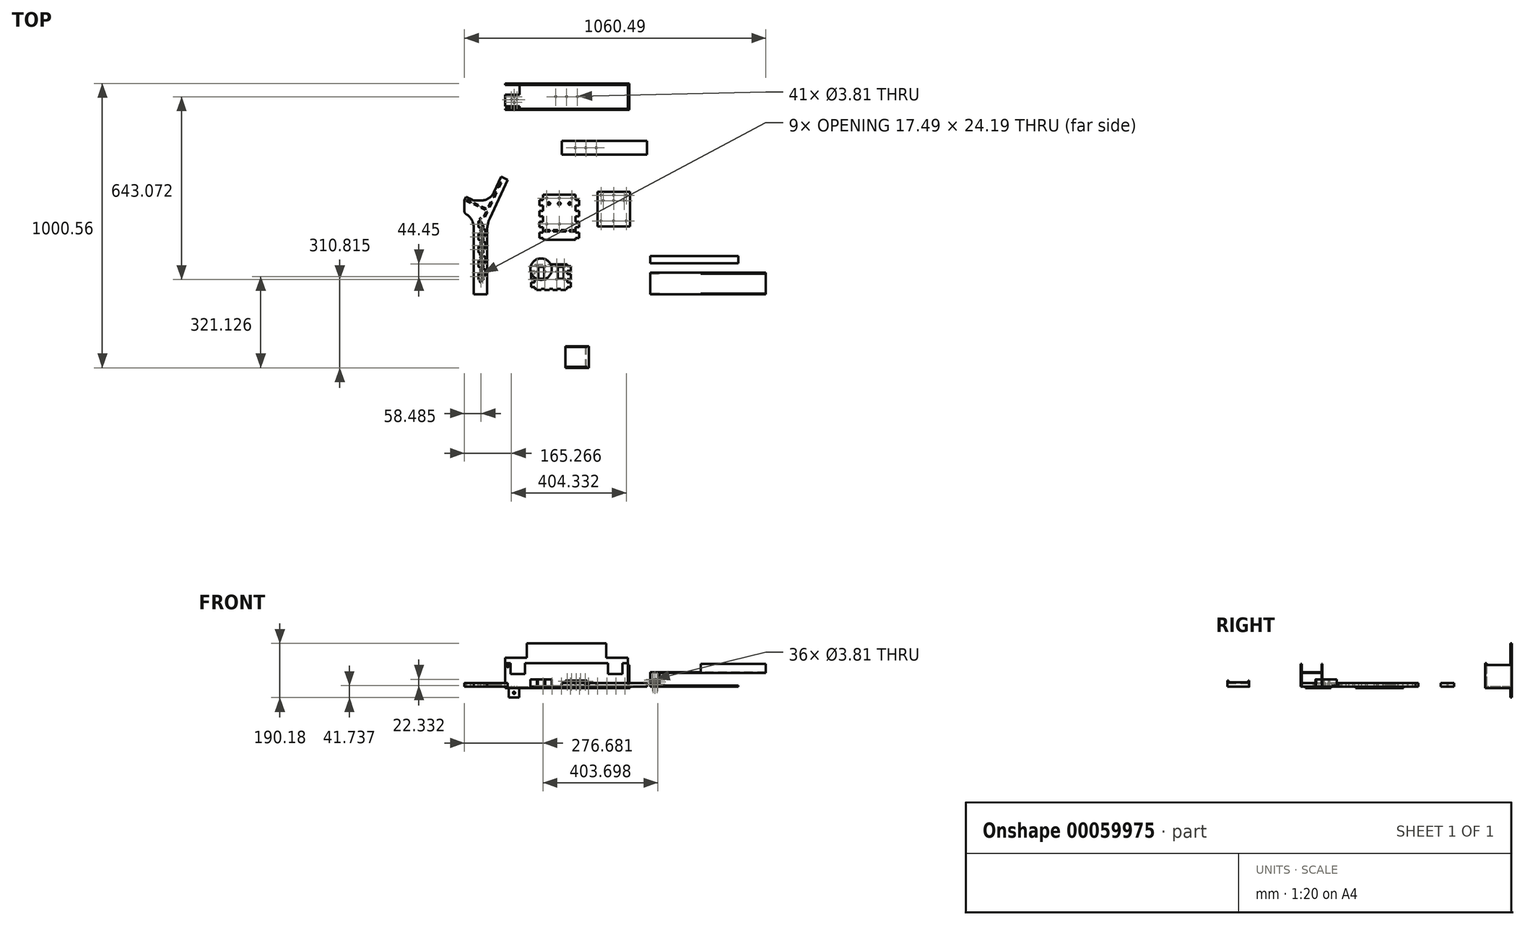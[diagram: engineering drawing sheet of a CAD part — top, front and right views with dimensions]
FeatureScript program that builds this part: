
annotation { "Feature Type Name" : "Feature", "Feature Type Description" : "" }
export const myFeature = defineFeature(function(context is Context, id is Id, definition is map)
    precondition{}
    {
        {
            var Q0;
            Q0=qCreatedBy(makeId("Top.planeOp"),FACE);
            var sketch = newSketch(context, id + "F0", { "sketchPlane" : qUnion([Q0])});
            skLineSegment(sketch, "E0.bottom", {"start": v(0, 0) * mm, "end": v(46.04, 0) * mm});
            skLineSegment(sketch, "E0.top", {"start": v(0, 304.8) * mm, "end": v(46.04, 304.8) * mm});
            skLineSegment(sketch, "E0.left", {"start": v(0, 0) * mm, "end": v(0, 304.8) * mm});
            skLineSegment(sketch, "E0.right", {"start": v(46.04, 0) * mm, "end": v(46.04, 304.8) * mm});
            skSolve(sketch);
        }
        {
            var Q0;
            Q0=makeQuery(id+"F0.imprint","IMPRINT",FACE,{"disambiguationData":[TD([[makeQuery(id+"F0.imprint","IMPRINT",EDGE,{"derivedFrom":sQuery(id+"F0.wireOp",EDGE,"E0.bottom")}),1.0]])]});
            extrude(context, id + "F1", {"entities" : qUnion([Q0]), "depth" : 12.7 * mm});
        }
        {
            var Q0;
            Q0=qCreatedBy(makeId("Top.planeOp"),FACE);
            var sketch = newSketch(context, id + "F2", { "sketchPlane" : qUnion([Q0])});
            skCircle(sketch, "E1", {"center": v(-119.77, 141.64) * mm, "radius": 9.53 * mm});
            skLineSegment(sketch, "E2", {"start": v(-119.77, 132.11) * mm, "end": v(-119.77, 113.06) * mm, "construction": true});
            skLineSegment(sketch, "E3", {"start": v(-119.77, 113.06) * mm, "end": v(-122.95, 113.06) * mm});
            skLineSegment(sketch, "E4", {"start": v(-122.95, 113.06) * mm, "end": v(-129.3, 141.64) * mm});
            skLineSegment(sketch, "E5.MirrorCS", {"start": v(-119.77, 113.06) * mm, "end": v(-116.6, 113.06) * mm});
            skLineSegment(sketch, "E6.MirrorCS", {"start": v(-116.6, 113.06) * mm, "end": v(-110.25, 141.64) * mm});
            skCircle(sketch, "E7", {"center": v(-119.77, 141.64) * mm, "radius": 1.9 * mm});
            skSolve(sketch);
        }
        {
            var Q0;
            Q0=qSketchRegion(id+"F2",true);
            extrude(context, id + "F3", {"entities" : qUnion([Q0]), "depth" : 12.7 * mm});
        }
        {
            var Q0;
            Q0=qCreatedBy(makeId("Top.planeOp"),FACE);
            var sketch = newSketch(context, id + "F4", { "sketchPlane" : qUnion([Q0])});
            skLineSegment(sketch, "E8.bottom", {"start": v(-408.15, 0) * mm, "end": v(-455.78, 0) * mm});
            skLineSegment(sketch, "E8.top", {"start": v(-408.15, 431.8) * mm, "end": v(-455.78, 431.8) * mm});
            skLineSegment(sketch, "E8.left", {"start": v(-408.15, 0) * mm, "end": v(-408.15, 431.8) * mm});
            skLineSegment(sketch, "E8.right", {"start": v(-455.78, 0) * mm, "end": v(-455.78, 279.4) * mm});
            skLineSegment(sketch, "E9", {"start": v(-455.78, 360.5) * mm, "end": v(-455.78, 360.5) * mm});
            skLineSegment(sketch, "E10", {"start": v(-455.78, 360.5) * mm, "end": v(-481.84, 288.89) * mm});
            skLineSegment(sketch, "E11", {"start": v(-481.84, 288.89) * mm, "end": v(-455.78, 279.4) * mm});
            skLineSegment(sketch, "E12", {"start": v(-455.78, 279.4) * mm, "end": v(-455.78, 360.5) * mm});
            skLineSegment(sketch, "E13", {"start": v(-455.78, 279.4) * mm, "end": v(-455.78, 431.8) * mm});
            skSolve(sketch);
        }
        {
            var Q0;
            Q0=makeQuery(id+"F4.imprint","IMPRINT",FACE,{"disambiguationData":[TD([[makeQuery(id+"F4.imprint","IMPRINT",EDGE,{"derivedFrom":sQuery(id+"F4.wireOp",EDGE,"E9")}),1.0]])]});
            var Q1;
            Q1=makeQuery(id+"F4.imprint","IMPRINT",FACE,{"disambiguationData":[TD([[makeQuery(id+"F4.imprint","IMPRINT",EDGE,{"derivedFrom":sQuery(id+"F4.wireOp",EDGE,"E8.bottom")}),-1.0]])]});
            var Q2;
            Q2=makeQuery(id+"F4.imprint","IMPRINT",FACE,{"disambiguationData":[TD([[makeQuery(id+"F4.imprint","IMPRINT",EDGE,{"derivedFrom":sQuery(id+"F4.wireOp",EDGE,"E10")}),1.0]])]});
            extrude(context, id + "F5", {"entities" : qUnion([Q0, Q1, Q2]), "depth" : 12.7 * mm});
        }
        {
            var Q0;
            Q0=makeQuery(id+"F5.opExtrude","SWEPT_FACE",FACE,{"disambiguationData":[OSD([sQuery(id+"F4.wireOp",EDGE,"E8.left")])]});
            var sketch = newSketch(context, id + "F6", { "sketchPlane" : qUnion([Q0])});
            skLineSegment(sketch, "E14.bottom", {"start": v(431.8, 12.7) * mm, "end": v(355.6, 12.7) * mm});
            skLineSegment(sketch, "E14.top", {"start": v(431.8, 0) * mm, "end": v(355.6, 0) * mm});
            skLineSegment(sketch, "E14.left", {"start": v(431.8, 12.7) * mm, "end": v(431.8, 0) * mm});
            skLineSegment(sketch, "E14.right", {"start": v(355.6, 12.7) * mm, "end": v(355.6, 0) * mm});
            skSolve(sketch);
        }
        {
            var Q0;
            Q0=makeQuery(id+"F6.imprint","IMPRINT",FACE,{"disambiguationData":[TD([[makeQuery(id+"F6.imprint","IMPRINT",EDGE,{"derivedFrom":sQuery(id+"F6.wireOp",EDGE,"E14.bottom")}),-1.0]])]});
            extrude(context, id + "F7", {"entities" : qUnion([Q0]), "operationType" : NewBodyOperationType.ADD, "depth" : 6.35 * mm});
        }
        {
            var Q0;
            Q0=makeQuery(id+"F5.opExtrude","CAP_FACE",FACE,{"disambiguationData":[OSD([sQuery(id+"F4.wireOp",EDGE,"E8.bottom"),sQuery(id+"F4.wireOp",EDGE,"E8.top"),sQuery(id+"F4.wireOp",EDGE,"E8.left"),sQuery(id+"F4.wireOp",EDGE,"E8.right"),sQuery(id+"F4.wireOp",EDGE,"E9"),sQuery(id+"F4.wireOp",EDGE,"E10"),sQuery(id+"F4.wireOp",EDGE,"E11")])],"isStart":false});
            var sketch = newSketch(context, id + "F8", { "sketchPlane" : qUnion([Q0])});
            skLineSegment(sketch, "E15", {"start": v(-473.7, 292.68) * mm, "end": v(-470.72, 291.6) * mm});
            skLineSegment(sketch, "E16", {"start": v(-470.72, 291.6) * mm, "end": v(-466.38, 303.53) * mm});
            skLineSegment(sketch, "E17", {"start": v(-466.38, 303.53) * mm, "end": v(-469.36, 304.62) * mm});
            skLineSegment(sketch, "E18", {"start": v(-465.02, 316.55) * mm, "end": v(-462.03, 315.46) * mm});
            skLineSegment(sketch, "E19", {"start": v(-462.03, 315.46) * mm, "end": v(-457.69, 327.4) * mm});
            skLineSegment(sketch, "E20", {"start": v(-457.69, 327.4) * mm, "end": v(-460.67, 328.48) * mm});
            skLineSegment(sketch, "E21", {"start": v(-456.33, 340.42) * mm, "end": v(-453.36, 339.34) * mm});
            skLineSegment(sketch, "E22", {"start": v(-453.36, 339.34) * mm, "end": v(-449.01, 351.27) * mm});
            skLineSegment(sketch, "E23", {"start": v(-449.01, 351.27) * mm, "end": v(-451.9, 352.61) * mm});
            skPoint(sketch, "E24.startSnap0", {"position": v(-459.86, 321.43) * mm});
            skLineSegment(sketch, "E25", {"start": v(-473.7, 292.68) * mm, "end": v(-469.36, 304.62) * mm});
            skLineSegment(sketch, "E26", {"start": v(-465.02, 316.55) * mm, "end": v(-460.67, 328.48) * mm});
            skLineSegment(sketch, "E27", {"start": v(-456.33, 340.42) * mm, "end": v(-451.9, 352.61) * mm});
            skLineSegment(sketch, "E28", {"start": v(-435.45, 314.23) * mm, "end": v(-423.52, 309.9) * mm});
            skLineSegment(sketch, "E29", {"start": v(-435.45, 314.23) * mm, "end": v(-436.54, 311.25) * mm});
            skLineSegment(sketch, "E30", {"start": v(-436.54, 311.25) * mm, "end": v(-424.6, 306.9) * mm});
            skLineSegment(sketch, "E31", {"start": v(-424.6, 306.9) * mm, "end": v(-423.52, 309.9) * mm});
            skLineSegment(sketch, "E32", {"start": v(-453.35, 320.75) * mm, "end": v(-441.42, 316.4) * mm});
            skLineSegment(sketch, "E33", {"start": v(-453.35, 320.75) * mm, "end": v(-454.44, 317.77) * mm});
            skLineSegment(sketch, "E34", {"start": v(-454.44, 317.77) * mm, "end": v(-442.5, 313.42) * mm});
            skLineSegment(sketch, "E35", {"start": v(-442.5, 313.42) * mm, "end": v(-441.42, 316.4) * mm});
            skLineSegment(sketch, "E36", {"start": v(-417.55, 307.72) * mm, "end": v(-405.61, 303.38) * mm});
            skLineSegment(sketch, "E37", {"start": v(-417.55, 307.72) * mm, "end": v(-418.63, 304.74) * mm});
            skLineSegment(sketch, "E38", {"start": v(-418.63, 304.74) * mm, "end": v(-406.7, 300.4) * mm});
            skLineSegment(sketch, "E39", {"start": v(-406.7, 300.4) * mm, "end": v(-405.61, 303.38) * mm});
            skSolve(sketch);
        }
        {
            var Q0;
            Q0=qSketchRegion(id+"F8",true);
            extrude(context, id + "F9", {"entities" : qUnion([Q0]), "operationType" : NewBodyOperationType.REMOVE, "endBound" : BoundingType.UP_TO_NEXT, "oppositeDirection" : true, "depth" : 25.4 * mm});
        }
        {
            var Q0;
            Q0=qCreatedBy(makeId("Top.planeOp"),FACE);
            var sketch = newSketch(context, id + "F10", { "sketchPlane" : qUnion([Q0])});
            skLineSegment(sketch, "E40.bottom", {"start": v(-574.22, 0) * mm, "end": v(-621.84, 0) * mm});
            skLineSegment(sketch, "E40.top", {"start": v(-574.22, 330.2) * mm, "end": v(-621.84, 330.2) * mm});
            skLineSegment(sketch, "E40.left", {"start": v(-574.22, 0) * mm, "end": v(-574.22, 330.2) * mm});
            skLineSegment(sketch, "E40.right", {"start": v(-621.84, 0) * mm, "end": v(-621.84, 330.2) * mm});
            skLineSegment(sketch, "E41", {"start": v(-574.22, 247.83) * mm, "end": v(-501.76, 403.22) * mm});
            skLineSegment(sketch, "E42", {"start": v(-501.76, 403.22) * mm, "end": v(-524.78, 413.95) * mm});
            skLineSegment(sketch, "E43", {"start": v(-524.78, 413.95) * mm, "end": v(-563.84, 330.2) * mm});
            skCircle(sketch, "E44", {"center": v(-598.03, 266.7) * mm, "radius": 1.84 * mm});
            skCircle(sketch, "E45", {"center": v(-598.03, 139.7) * mm, "radius": 1.84 * mm});
            skCircle(sketch, "E46", {"center": v(-598.03, 44.45) * mm, "radius": 1.84 * mm});
            skLineSegment(sketch, "E47", {"start": v(-574.22, 165.1) * mm, "end": v(-621.84, 165.1) * mm, "construction": true});
            skLineSegment(sketch, "E48", {"start": v(-574.22, 247.83) * mm, "end": v(-671.77, 293.32) * mm});
            skLineSegment(sketch, "E49", {"start": v(-671.77, 293.32) * mm, "end": v(-648.73, 342.73) * mm});
            skLineSegment(sketch, "E50", {"start": v(-648.73, 342.73) * mm, "end": v(-621.84, 330.2) * mm});
            skLineSegment(sketch, "E51", {"start": v(-598.03, 330.2) * mm, "end": v(-598.03, 0) * mm, "construction": true});
            skLineSegment(sketch, "E52", {"start": v(-654.1, 331.22) * mm, "end": v(-654.1, 285.08) * mm});
            skLineSegment(sketch, "E53", {"start": v(-574.22, 330.2) * mm, "end": v(-563.84, 330.2) * mm});
            skSolve(sketch);
        }
        {
            var Q0;
            {var subQ0=sQuery(id+"F10.wireOp",EDGE,"E50");Q0=makeQuery(id+"F10.imprint","IMPRINT",FACE,{"disambiguationData":[TD([[makeQuery(id+"F10.imprint","IMPRINT",EDGE,{"derivedFrom":subQ0}),-1.0]])]});}
            var Q1;
            Q1=makeQuery(id+"F10.imprint","IMPRINT",FACE,{"disambiguationData":[TD([[makeQuery(id+"F10.imprint","IMPRINT",EDGE,{"derivedFrom":sQuery(id+"F10.wireOp",EDGE,"E44")}),-1.0]])]});
            var Q2;
            {var subQ0=sQuery(id+"F10.wireOp",EDGE,"E41");Q2=makeQuery(id+"F10.imprint","IMPRINT",FACE,{"disambiguationData":[TD([[makeQuery(id+"F10.imprint","IMPRINT",EDGE,{"derivedFrom":subQ0}),1.0]])]});}
            var Q3;
            {var subQ1=sQuery(id+"F10.wireOp",EDGE,"E40.bottom");Q3=makeQuery(id+"F10.imprint","IMPRINT",FACE,{"disambiguationData":[TD([[makeQuery(id+"F10.imprint","IMPRINT",EDGE,{"derivedFrom":subQ1}),-1.0]])]});}
            extrude(context, id + "F11", {"entities" : qUnion([Q0, Q1, Q2, Q3]), "depth" : 12.7 * mm});
        }
        {
            var Q0;
            Q0=makeQuery(id+"F5.opExtrude","SWEPT_BODY",BODY,{"disambiguationData":[OSD([sQuery(id+"F4.wireOp",EDGE,"E8.bottom"),sQuery(id+"F4.wireOp",EDGE,"E8.top"),sQuery(id+"F4.wireOp",EDGE,"E8.left"),sQuery(id+"F4.wireOp",EDGE,"E8.right"),sQuery(id+"F4.wireOp",EDGE,"E10"),sQuery(id+"F4.wireOp",EDGE,"E11"),sQuery(id+"F4.wireOp",EDGE,"E13")])]});
            deleteBodies(context, id + "F12", {"entities" : qUnion([Q0])});
        }
        {
            var Q0;
            Q0=makeQuery(id+"F11.opExtrude","CAP_FACE",FACE,{"disambiguationData":[OSD([sQuery(id+"F10.wireOp",EDGE,"E40.bottom"),sQuery(id+"F10.wireOp",EDGE,"E40.top"),sQuery(id+"F10.wireOp",EDGE,"E40.left"),sQuery(id+"F10.wireOp",EDGE,"E40.right"),sQuery(id+"F10.wireOp",EDGE,"Y91T5dXO-O9do-Qezp-Nh4v-n6mu9yF64eSj"),sQuery(id+"F10.wireOp",EDGE,"wk8H9K5M-Q0OB-IsqO-xqjk-N4ZivMZWohHq"),sQuery(id+"F10.wireOp",EDGE,"1UNdf9ru-KzUG-1IXl-ZwoR-ekO7E109dlTN"),sQuery(id+"F10.wireOp",EDGE,"abHQwaP6-kXHW-M4Kr-ZBDh-lSKwXKwhMN8O")])],"isStart":false});
            var sketch = newSketch(context, id + "F13", { "sketchPlane" : qUnion([Q0])});
            skLineSegment(sketch, "E54.bottom", {"start": v(-604.35, 88.9) * mm, "end": v(-580.57, 88.9) * mm});
            skLineSegment(sketch, "E54.top", {"start": v(-604.35, 50.8) * mm, "end": v(-580.57, 50.8) * mm});
            skLineSegment(sketch, "E54.left", {"start": v(-604.35, 88.9) * mm, "end": v(-604.35, 50.8) * mm});
            skLineSegment(sketch, "E54.right", {"start": v(-580.57, 88.9) * mm, "end": v(-580.57, 50.8) * mm});
            skLineSegment(sketch, "E55", {"start": v(-604.35, 82.9) * mm, "end": v(-584.31, 50.8) * mm});
            skLineSegment(sketch, "E56", {"start": v(-600.6, 88.9) * mm, "end": v(-580.57, 56.8) * mm});
            skLineSegment(sketch, "E57.0.1.0", {"start": v(-604.35, 133.35) * mm, "end": v(-580.57, 133.35) * mm});
            skLineSegment(sketch, "E57.0.1.1", {"start": v(-580.57, 133.35) * mm, "end": v(-580.57, 95.25) * mm});
            skLineSegment(sketch, "E57.0.1.2", {"start": v(-604.35, 127.35) * mm, "end": v(-584.31, 95.25) * mm});
            skLineSegment(sketch, "E57.0.1.3", {"start": v(-604.35, 95.25) * mm, "end": v(-580.57, 95.25) * mm});
            skLineSegment(sketch, "E57.0.1.4", {"start": v(-604.35, 133.35) * mm, "end": v(-604.35, 95.25) * mm});
            skLineSegment(sketch, "E57.0.1.5", {"start": v(-600.6, 133.35) * mm, "end": v(-580.57, 101.25) * mm});
            skLineSegment(sketch, "E57.direction1", {"start": v(-604.35, 88.9) * mm, "end": v(-529.02, 88.9) * mm, "construction": true});
            skLineSegment(sketch, "E57.direction2", {"start": v(-604.35, 88.9) * mm, "end": v(-604.35, 133.35) * mm, "construction": true});
            skLineSegment(sketch, "E58.0.1.0", {"start": v(-604.35, 184.15) * mm, "end": v(-580.57, 184.15) * mm});
            skLineSegment(sketch, "E58.0.1.1", {"start": v(-580.57, 184.15) * mm, "end": v(-580.57, 146.05) * mm});
            skLineSegment(sketch, "E58.0.1.2", {"start": v(-604.35, 178.15) * mm, "end": v(-584.31, 146.05) * mm});
            skLineSegment(sketch, "E58.0.1.3", {"start": v(-604.35, 146.05) * mm, "end": v(-580.57, 146.05) * mm});
            skLineSegment(sketch, "E58.0.1.4", {"start": v(-604.35, 184.15) * mm, "end": v(-604.35, 146.05) * mm});
            skLineSegment(sketch, "E58.0.1.5", {"start": v(-600.6, 184.15) * mm, "end": v(-580.57, 152.05) * mm});
            skLineSegment(sketch, "E58.0.1.6", {"start": v(-604.35, 139.7) * mm, "end": v(-604.35, 184.15) * mm, "construction": true});
            skLineSegment(sketch, "E58.direction1", {"start": v(-604.35, 133.35) * mm, "end": v(-529.02, 133.35) * mm, "construction": true});
            skLineSegment(sketch, "E58.direction2", {"start": v(-604.35, 133.35) * mm, "end": v(-604.35, 184.15) * mm, "construction": true});
            skLineSegment(sketch, "E59.0.1.0", {"start": v(-604.35, 228.6) * mm, "end": v(-580.57, 228.6) * mm});
            skLineSegment(sketch, "E59.0.1.1", {"start": v(-600.6, 228.6) * mm, "end": v(-580.57, 196.5) * mm});
            skLineSegment(sketch, "E59.0.1.2", {"start": v(-580.57, 228.6) * mm, "end": v(-580.57, 190.5) * mm});
            skLineSegment(sketch, "E59.0.1.3", {"start": v(-604.35, 190.5) * mm, "end": v(-580.57, 190.5) * mm});
            skLineSegment(sketch, "E59.0.1.4", {"start": v(-604.35, 228.6) * mm, "end": v(-604.35, 190.5) * mm});
            skLineSegment(sketch, "E59.0.1.5", {"start": v(-604.35, 222.6) * mm, "end": v(-584.31, 190.5) * mm});
            skLineSegment(sketch, "E59.0.2.0", {"start": v(-604.35, 273.05) * mm, "end": v(-580.57, 273.05) * mm});
            skLineSegment(sketch, "E59.0.2.1", {"start": v(-600.6, 273.05) * mm, "end": v(-580.57, 240.95) * mm});
            skLineSegment(sketch, "E59.0.2.2", {"start": v(-580.57, 273.05) * mm, "end": v(-580.57, 234.95) * mm});
            skLineSegment(sketch, "E59.0.2.3", {"start": v(-604.35, 234.95) * mm, "end": v(-580.57, 234.95) * mm});
            skLineSegment(sketch, "E59.0.2.4", {"start": v(-604.35, 273.05) * mm, "end": v(-604.35, 234.95) * mm});
            skLineSegment(sketch, "E59.0.2.5", {"start": v(-604.35, 267.05) * mm, "end": v(-584.31, 234.95) * mm});
            skLineSegment(sketch, "E59.direction1", {"start": v(-604.35, 184.15) * mm, "end": v(-529.02, 184.15) * mm, "construction": true});
            skLineSegment(sketch, "E59.direction2", {"start": v(-604.35, 184.15) * mm, "end": v(-604.35, 228.6) * mm, "construction": true});
            skSolve(sketch);
        }
        {
            var Q0;
            {var subQ3=sQuery(id+"F13.wireOp",EDGE,"E59.0.2.5");Q0=makeQuery(id+"F13.imprint","IMPRINT",FACE,{"disambiguationData":[TD([[makeQuery(id+"F13.imprint","IMPRINT",EDGE,{"derivedFrom":subQ3}),-1.0]])]});}
            var Q1;
            {var subQ3=sQuery(id+"F13.wireOp",EDGE,"E59.0.1.1");Q1=makeQuery(id+"F13.imprint","IMPRINT",FACE,{"disambiguationData":[TD([[makeQuery(id+"F13.imprint","IMPRINT",EDGE,{"derivedFrom":subQ3}),1.0]])]});}
            var Q2;
            {var subQ3=sQuery(id+"F13.wireOp",EDGE,"E59.0.1.5");Q2=makeQuery(id+"F13.imprint","IMPRINT",FACE,{"disambiguationData":[TD([[makeQuery(id+"F13.imprint","IMPRINT",EDGE,{"derivedFrom":subQ3}),-1.0]])]});}
            var Q3;
            {var subQ3=sQuery(id+"F13.wireOp",EDGE,"E58.0.1.5");Q3=makeQuery(id+"F13.imprint","IMPRINT",FACE,{"disambiguationData":[TD([[makeQuery(id+"F13.imprint","IMPRINT",EDGE,{"derivedFrom":subQ3}),1.0]])]});}
            var Q4;
            {var subQ0=sQuery(id+"F13.wireOp",EDGE,"E58.0.1.2");Q4=makeQuery(id+"F13.imprint","IMPRINT",FACE,{"disambiguationData":[TD([[makeQuery(id+"F13.imprint","IMPRINT",EDGE,{"derivedFrom":subQ0}),-1.0]])]});}
            var Q5;
            {var subQ3=sQuery(id+"F13.wireOp",EDGE,"E57.0.1.5");Q5=makeQuery(id+"F13.imprint","IMPRINT",FACE,{"disambiguationData":[TD([[makeQuery(id+"F13.imprint","IMPRINT",EDGE,{"derivedFrom":subQ3}),1.0]])]});}
            var Q6;
            {var subQ0=sQuery(id+"F13.wireOp",EDGE,"E57.0.1.2");Q6=makeQuery(id+"F13.imprint","IMPRINT",FACE,{"disambiguationData":[TD([[makeQuery(id+"F13.imprint","IMPRINT",EDGE,{"derivedFrom":subQ0}),-1.0]])]});}
            var Q7;
            {var subQ3=sQuery(id+"F13.wireOp",EDGE,"E56");Q7=makeQuery(id+"F13.imprint","IMPRINT",FACE,{"disambiguationData":[TD([[makeQuery(id+"F13.imprint","IMPRINT",EDGE,{"derivedFrom":subQ3}),1.0]])]});}
            var Q8;
            {var subQ3=sQuery(id+"F13.wireOp",EDGE,"E55");Q8=makeQuery(id+"F13.imprint","IMPRINT",FACE,{"disambiguationData":[TD([[makeQuery(id+"F13.imprint","IMPRINT",EDGE,{"derivedFrom":subQ3}),-1.0]])]});}
            extrude(context, id + "F14", {"entities" : qUnion([Q0, Q1, Q2, Q3, Q4, Q5, Q6, Q7, Q8]), "operationType" : NewBodyOperationType.REMOVE, "endBound" : BoundingType.UP_TO_NEXT, "oppositeDirection" : true, "depth" : 25.4 * mm});
        }
        {
            var Q0;
            Q0=makeQuery(id+"F14.boolean.opBoolean","COPY",EDGE,{"derivedFrom":makeQuery(id+"F14.opExtrude","SWEPT_EDGE",EDGE,{"disambiguationData":[OSD([sQuery(id+"F13.wireOp",EDGE,"E59.0.2.3"),sQuery(id+"F13.wireOp",EDGE,"E59.0.2.4")])]})});
            var Q1;
            Q1=makeQuery(id+"F14.boolean.opBoolean","COPY",EDGE,{"derivedFrom":makeQuery(id+"F14.opExtrude","SWEPT_EDGE",EDGE,{"disambiguationData":[OSD([sQuery(id+"F13.wireOp",EDGE,"E59.0.1.3"),sQuery(id+"F13.wireOp",EDGE,"E59.0.1.4")])]})});
            var Q2;
            Q2=makeQuery(id+"F14.boolean.opBoolean","COPY",EDGE,{"derivedFrom":makeQuery(id+"F14.opExtrude","SWEPT_EDGE",EDGE,{"disambiguationData":[OSD([sQuery(id+"F13.wireOp",EDGE,"E58.0.1.3"),sQuery(id+"F13.wireOp",EDGE,"E58.0.1.4")])]})});
            var Q3;
            Q3=makeQuery(id+"F14.boolean.opBoolean","COPY",EDGE,{"derivedFrom":makeQuery(id+"F14.opExtrude","SWEPT_EDGE",EDGE,{"disambiguationData":[OSD([sQuery(id+"F13.wireOp",EDGE,"E57.0.1.3"),sQuery(id+"F13.wireOp",EDGE,"E57.0.1.4")])]})});
            var Q4;
            Q4=makeQuery(id+"F14.boolean.opBoolean","COPY",EDGE,{"derivedFrom":makeQuery(id+"F14.opExtrude","SWEPT_EDGE",EDGE,{"disambiguationData":[OSD([sQuery(id+"F13.wireOp",EDGE,"E54.top"),sQuery(id+"F13.wireOp",EDGE,"E54.left")])]})});
            var Q5;
            Q5=makeQuery(id+"F14.boolean.opBoolean","COPY",EDGE,{"derivedFrom":makeQuery(id+"F14.opExtrude","SWEPT_EDGE",EDGE,{"disambiguationData":[OSD([sQuery(id+"F13.wireOp",EDGE,"E54.left"),sQuery(id+"F13.wireOp",EDGE,"E55")])]})});
            var Q6;
            Q6=makeQuery(id+"F14.boolean.opBoolean","COPY",EDGE,{"derivedFrom":makeQuery(id+"F14.opExtrude","SWEPT_EDGE",EDGE,{"disambiguationData":[OSD([sQuery(id+"F13.wireOp",EDGE,"E57.0.1.2"),sQuery(id+"F13.wireOp",EDGE,"E57.0.1.4")])]})});
            var Q7;
            Q7=makeQuery(id+"F14.boolean.opBoolean","COPY",EDGE,{"derivedFrom":makeQuery(id+"F14.opExtrude","SWEPT_EDGE",EDGE,{"disambiguationData":[OSD([sQuery(id+"F13.wireOp",EDGE,"E58.0.1.2"),sQuery(id+"F13.wireOp",EDGE,"E58.0.1.4")])]})});
            var Q8;
            Q8=makeQuery(id+"F14.boolean.opBoolean","COPY",EDGE,{"derivedFrom":makeQuery(id+"F14.opExtrude","SWEPT_EDGE",EDGE,{"disambiguationData":[OSD([sQuery(id+"F13.wireOp",EDGE,"E59.0.1.4"),sQuery(id+"F13.wireOp",EDGE,"E59.0.1.5")])]})});
            var Q9;
            Q9=makeQuery(id+"F14.boolean.opBoolean","COPY",EDGE,{"derivedFrom":makeQuery(id+"F14.opExtrude","SWEPT_EDGE",EDGE,{"disambiguationData":[OSD([sQuery(id+"F13.wireOp",EDGE,"E59.0.2.4"),sQuery(id+"F13.wireOp",EDGE,"E59.0.2.5")])]})});
            var Q10;
            Q10=makeQuery(id+"F14.boolean.opBoolean","COPY",EDGE,{"derivedFrom":makeQuery(id+"F14.opExtrude","SWEPT_EDGE",EDGE,{"disambiguationData":[OSD([sQuery(id+"F13.wireOp",EDGE,"E54.bottom"),sQuery(id+"F13.wireOp",EDGE,"E54.right")])]})});
            var Q11;
            Q11=makeQuery(id+"F14.boolean.opBoolean","COPY",EDGE,{"derivedFrom":makeQuery(id+"F14.opExtrude","SWEPT_EDGE",EDGE,{"disambiguationData":[OSD([sQuery(id+"F13.wireOp",EDGE,"E57.0.1.0"),sQuery(id+"F13.wireOp",EDGE,"E57.0.1.1")])]})});
            var Q12;
            Q12=makeQuery(id+"F14.boolean.opBoolean","COPY",EDGE,{"derivedFrom":makeQuery(id+"F14.opExtrude","SWEPT_EDGE",EDGE,{"disambiguationData":[OSD([sQuery(id+"F13.wireOp",EDGE,"E58.0.1.0"),sQuery(id+"F13.wireOp",EDGE,"E58.0.1.1")])]})});
            var Q13;
            Q13=makeQuery(id+"F14.boolean.opBoolean","COPY",EDGE,{"derivedFrom":makeQuery(id+"F14.opExtrude","SWEPT_EDGE",EDGE,{"disambiguationData":[OSD([sQuery(id+"F13.wireOp",EDGE,"E59.0.1.0"),sQuery(id+"F13.wireOp",EDGE,"E59.0.1.2")])]})});
            var Q14;
            Q14=makeQuery(id+"F14.boolean.opBoolean","COPY",EDGE,{"derivedFrom":makeQuery(id+"F14.opExtrude","SWEPT_EDGE",EDGE,{"disambiguationData":[OSD([sQuery(id+"F13.wireOp",EDGE,"E59.0.1.1"),sQuery(id+"F13.wireOp",EDGE,"E59.0.1.2")])]})});
            var Q15;
            Q15=makeQuery(id+"F14.boolean.opBoolean","COPY",EDGE,{"derivedFrom":makeQuery(id+"F14.opExtrude","SWEPT_EDGE",EDGE,{"disambiguationData":[OSD([sQuery(id+"F13.wireOp",EDGE,"E58.0.1.1"),sQuery(id+"F13.wireOp",EDGE,"E58.0.1.5")])]})});
            var Q16;
            Q16=makeQuery(id+"F14.boolean.opBoolean","COPY",EDGE,{"derivedFrom":makeQuery(id+"F14.opExtrude","SWEPT_EDGE",EDGE,{"disambiguationData":[OSD([sQuery(id+"F13.wireOp",EDGE,"E57.0.1.1"),sQuery(id+"F13.wireOp",EDGE,"E57.0.1.5")])]})});
            var Q17;
            Q17=makeQuery(id+"F14.boolean.opBoolean","COPY",EDGE,{"derivedFrom":makeQuery(id+"F14.opExtrude","SWEPT_EDGE",EDGE,{"disambiguationData":[OSD([sQuery(id+"F13.wireOp",EDGE,"E54.right"),sQuery(id+"F13.wireOp",EDGE,"E56")])]})});
            var Q18;
            Q18=makeQuery(id+"F14.boolean.opBoolean","COPY",EDGE,{"derivedFrom":makeQuery(id+"F14.opExtrude","SWEPT_EDGE",EDGE,{"disambiguationData":[OSD([sQuery(id+"F13.wireOp",EDGE,"E54.top"),sQuery(id+"F13.wireOp",EDGE,"E55")])]})});
            var Q19;
            Q19=makeQuery(id+"F14.boolean.opBoolean","COPY",EDGE,{"derivedFrom":makeQuery(id+"F14.opExtrude","SWEPT_EDGE",EDGE,{"disambiguationData":[OSD([sQuery(id+"F13.wireOp",EDGE,"E57.0.1.2"),sQuery(id+"F13.wireOp",EDGE,"E57.0.1.3")])]})});
            var Q20;
            Q20=makeQuery(id+"F14.boolean.opBoolean","COPY",EDGE,{"derivedFrom":makeQuery(id+"F14.opExtrude","SWEPT_EDGE",EDGE,{"disambiguationData":[OSD([sQuery(id+"F13.wireOp",EDGE,"E58.0.1.2"),sQuery(id+"F13.wireOp",EDGE,"E58.0.1.3")])]})});
            var Q21;
            Q21=makeQuery(id+"F14.boolean.opBoolean","COPY",EDGE,{"derivedFrom":makeQuery(id+"F14.opExtrude","SWEPT_EDGE",EDGE,{"disambiguationData":[OSD([sQuery(id+"F13.wireOp",EDGE,"E59.0.1.3"),sQuery(id+"F13.wireOp",EDGE,"E59.0.1.5")])]})});
            var Q22;
            Q22=makeQuery(id+"F14.boolean.opBoolean","COPY",EDGE,{"derivedFrom":makeQuery(id+"F14.opExtrude","SWEPT_EDGE",EDGE,{"disambiguationData":[OSD([sQuery(id+"F13.wireOp",EDGE,"E59.0.2.3"),sQuery(id+"F13.wireOp",EDGE,"E59.0.2.5")])]})});
            var Q23;
            Q23=makeQuery(id+"F14.boolean.opBoolean","COPY",EDGE,{"derivedFrom":makeQuery(id+"F14.opExtrude","SWEPT_EDGE",EDGE,{"disambiguationData":[OSD([sQuery(id+"F13.wireOp",EDGE,"E54.bottom"),sQuery(id+"F13.wireOp",EDGE,"E56")])]})});
            var Q24;
            Q24=makeQuery(id+"F14.boolean.opBoolean","COPY",EDGE,{"derivedFrom":makeQuery(id+"F14.opExtrude","SWEPT_EDGE",EDGE,{"disambiguationData":[OSD([sQuery(id+"F13.wireOp",EDGE,"E57.0.1.0"),sQuery(id+"F13.wireOp",EDGE,"E57.0.1.5")])]})});
            var Q25;
            Q25=makeQuery(id+"F14.boolean.opBoolean","COPY",EDGE,{"derivedFrom":makeQuery(id+"F14.opExtrude","SWEPT_EDGE",EDGE,{"disambiguationData":[OSD([sQuery(id+"F13.wireOp",EDGE,"E58.0.1.0"),sQuery(id+"F13.wireOp",EDGE,"E58.0.1.5")])]})});
            var Q26;
            Q26=makeQuery(id+"F14.boolean.opBoolean","COPY",EDGE,{"derivedFrom":makeQuery(id+"F14.opExtrude","SWEPT_EDGE",EDGE,{"disambiguationData":[OSD([sQuery(id+"F13.wireOp",EDGE,"E59.0.1.0"),sQuery(id+"F13.wireOp",EDGE,"E59.0.1.1")])]})});
            fillet(context, id + "F15", {"entities" : qUnion([Q0, Q1, Q2, Q3, Q4, Q5, Q6, Q7, Q8, Q9, Q10, Q11, Q12, Q13, Q14, Q15, Q16, Q17, Q18, Q19, Q20, Q21, Q22, Q23, Q24, Q25, Q26]), "radius" : 3.17 * mm, "tangentPropagation" : true, "allowEdgeOverflow" : false});
        }
        {
            var Q0;
            Q0=makeQuery(id+"F1.opExtrude","SWEPT_BODY",BODY,{"disambiguationData":[OSD([sQuery(id+"F0.wireOp",EDGE,"E0.bottom"),sQuery(id+"F0.wireOp",EDGE,"E0.top"),sQuery(id+"F0.wireOp",EDGE,"E0.left"),sQuery(id+"F0.wireOp",EDGE,"E0.right")])]});
            var Q1;
            Q1=makeQuery(id+"F1OaYgbKn4OfgPz_1.opExtrude","SWEPT_BODY",BODY,{"disambiguationData":[OSD([sQuery(id+"FSCGUaJBi3wnmaW_1.wireOp",EDGE,"10d2bce9-ad60-4194-9a44-aa3babc14cea.bottom"),sQuery(id+"FSCGUaJBi3wnmaW_1.wireOp",EDGE,"10d2bce9-ad60-4194-9a44-aa3babc14cea.top"),sQuery(id+"FSCGUaJBi3wnmaW_1.wireOp",EDGE,"10d2bce9-ad60-4194-9a44-aa3babc14cea.left"),sQuery(id+"FSCGUaJBi3wnmaW_1.wireOp",EDGE,"10d2bce9-ad60-4194-9a44-aa3babc14cea.right")])]});
            var Q2;
            Q2=makeQuery(id+"F3.opExtrude","SWEPT_BODY",BODY,{"disambiguationData":[OSD([sQuery(id+"F2.wireOp",EDGE,"E1"),sQuery(id+"F2.wireOp",EDGE,"E3"),sQuery(id+"F2.wireOp",EDGE,"E4"),sQuery(id+"F2.wireOp",EDGE,"E5.MirrorCS"),sQuery(id+"F2.wireOp",EDGE,"E6.MirrorCS"),sQuery(id+"F2.wireOp",EDGE,"E7")])]});
            deleteBodies(context, id + "F16", {"entities" : qUnion([Q0, Q1, Q2])});
        }
        {
            var Q0;
            Q0=makeQuery(id+"F11.opExtrude","CAP_FACE",FACE,{"disambiguationData":[OSD([sQuery(id+"F10.wireOp",EDGE,"E40.bottom"),sQuery(id+"F10.wireOp",EDGE,"E40.left"),sQuery(id+"F10.wireOp",EDGE,"E40.right"),sQuery(id+"F10.wireOp",EDGE,"E41"),sQuery(id+"F10.wireOp",EDGE,"E42"),sQuery(id+"F10.wireOp",EDGE,"E43"),sQuery(id+"F10.wireOp",EDGE,"E44"),sQuery(id+"F10.wireOp",EDGE,"E45"),sQuery(id+"F10.wireOp",EDGE,"E46")])],"isStart":false});
            var sketch = newSketch(context, id + "F17", { "sketchPlane" : qUnion([Q0])});
            skLineSegment(sketch, "E60", {"start": v(-519.03, 411.27) * mm, "end": v(-634.58, 163.46) * mm, "construction": true});
            skLineSegment(sketch, "E61", {"start": v(-527.08, 394) * mm, "end": v(-529.06, 394.93) * mm});
            skLineSegment(sketch, "E62", {"start": v(-529.06, 394.93) * mm, "end": v(-537.1, 377.66) * mm});
            skLineSegment(sketch, "E63", {"start": v(-537.1, 377.66) * mm, "end": v(-535.13, 376.74) * mm});
            skLineSegment(sketch, "E64.MirrorCS", {"start": v(-525.1, 393.08) * mm, "end": v(-533.15, 375.82) * mm});
            skLineSegment(sketch, "E65.MirrorCS", {"start": v(-527.08, 394) * mm, "end": v(-525.1, 393.08) * mm});
            skLineSegment(sketch, "E66.MirrorCS", {"start": v(-533.15, 375.82) * mm, "end": v(-535.13, 376.74) * mm});
            skLineSegment(sketch, "E67.1.0.0", {"start": v(-545.16, 360.4) * mm, "end": v(-553.2, 343.13) * mm});
            skLineSegment(sketch, "E67.1.0.1", {"start": v(-543.18, 359.48) * mm, "end": v(-545.16, 360.4) * mm});
            skLineSegment(sketch, "E67.1.0.2", {"start": v(-543.18, 359.48) * mm, "end": v(-541.2, 358.55) * mm});
            skLineSegment(sketch, "E67.1.0.3", {"start": v(-541.2, 358.55) * mm, "end": v(-549.25, 341.29) * mm});
            skLineSegment(sketch, "E67.1.0.4", {"start": v(-549.25, 341.29) * mm, "end": v(-551.23, 342.21) * mm});
            skLineSegment(sketch, "E67.1.0.5", {"start": v(-553.2, 343.13) * mm, "end": v(-551.23, 342.21) * mm});
            skLineSegment(sketch, "E67.2.0.0", {"start": v(-561.26, 325.87) * mm, "end": v(-569.31, 308.6) * mm});
            skLineSegment(sketch, "E67.2.0.1", {"start": v(-559.28, 324.95) * mm, "end": v(-561.26, 325.87) * mm});
            skLineSegment(sketch, "E67.2.0.2", {"start": v(-559.28, 324.95) * mm, "end": v(-557.3, 324.02) * mm});
            skLineSegment(sketch, "E67.2.0.3", {"start": v(-557.3, 324.02) * mm, "end": v(-565.35, 306.76) * mm});
            skLineSegment(sketch, "E67.2.0.4", {"start": v(-565.35, 306.76) * mm, "end": v(-567.33, 307.68) * mm});
            skLineSegment(sketch, "E67.2.0.5", {"start": v(-569.31, 308.6) * mm, "end": v(-567.33, 307.68) * mm});
            skLineSegment(sketch, "E67.direction1", {"start": v(-537.1, 377.66) * mm, "end": v(-553.2, 343.13) * mm, "construction": true});
            skLineSegment(sketch, "E68.0.3.0", {"start": v(-577.36, 291.34) * mm, "end": v(-585.41, 274.07) * mm});
            skLineSegment(sketch, "E68.3.3.0", {"start": v(-575.38, 290.41) * mm, "end": v(-577.36, 291.34) * mm});
            skLineSegment(sketch, "E68.6.3.0", {"start": v(-575.38, 290.41) * mm, "end": v(-573.4, 289.5) * mm});
            skLineSegment(sketch, "E68.9.3.0", {"start": v(-573.4, 289.5) * mm, "end": v(-581.46, 272.23) * mm});
            skLineSegment(sketch, "E68.12.3.0", {"start": v(-581.46, 272.23) * mm, "end": v(-583.43, 273.15) * mm});
            skLineSegment(sketch, "E68.15.3.0", {"start": v(-585.41, 274.07) * mm, "end": v(-583.43, 273.15) * mm});
            skLineSegment(sketch, "E69", {"start": v(-652.75, 334.1) * mm, "end": v(-555.2, 288.61) * mm, "construction": true});
            skLineSegment(sketch, "E70", {"start": v(-595.2, 307.27) * mm, "end": v(-594.28, 309.24) * mm});
            skLineSegment(sketch, "E71", {"start": v(-594.28, 309.24) * mm, "end": v(-578.74, 302) * mm});
            skLineSegment(sketch, "E72", {"start": v(-578.74, 302) * mm, "end": v(-579.66, 300.02) * mm});
            skLineSegment(sketch, "E73.MirrorCS", {"start": v(-596.12, 305.29) * mm, "end": v(-580.58, 298.04) * mm});
            skLineSegment(sketch, "E74.MirrorCS", {"start": v(-580.58, 298.04) * mm, "end": v(-579.66, 300.02) * mm});
            skLineSegment(sketch, "E75.MirrorCS", {"start": v(-595.2, 307.27) * mm, "end": v(-596.12, 305.29) * mm});
            skLineSegment(sketch, "E76.1.0.0", {"start": v(-620.18, 321.32) * mm, "end": v(-604.64, 314.07) * mm});
            skLineSegment(sketch, "E76.1.0.1", {"start": v(-621.1, 319.34) * mm, "end": v(-620.18, 321.32) * mm});
            skLineSegment(sketch, "E76.1.0.2", {"start": v(-621.1, 319.34) * mm, "end": v(-622.02, 317.36) * mm});
            skLineSegment(sketch, "E76.1.0.3", {"start": v(-622.02, 317.36) * mm, "end": v(-606.48, 310.12) * mm});
            skLineSegment(sketch, "E76.1.0.4", {"start": v(-606.48, 310.12) * mm, "end": v(-605.56, 312.1) * mm});
            skLineSegment(sketch, "E76.1.0.5", {"start": v(-604.64, 314.07) * mm, "end": v(-605.56, 312.1) * mm});
            skLineSegment(sketch, "E76.direction1", {"start": v(-594.28, 309.24) * mm, "end": v(-620.18, 321.32) * mm, "construction": true});
            skLineSegment(sketch, "E77.0.2.0", {"start": v(-646.07, 333.4) * mm, "end": v(-630.53, 326.15) * mm});
            skLineSegment(sketch, "E77.3.2.0", {"start": v(-647, 331.42) * mm, "end": v(-646.07, 333.4) * mm});
            skLineSegment(sketch, "E77.6.2.0", {"start": v(-647, 331.42) * mm, "end": v(-647.92, 329.44) * mm});
            skLineSegment(sketch, "E77.9.2.0", {"start": v(-647.92, 329.44) * mm, "end": v(-632.38, 322.2) * mm});
            skLineSegment(sketch, "E77.12.2.0", {"start": v(-632.38, 322.2) * mm, "end": v(-631.46, 324.17) * mm});
            skLineSegment(sketch, "E77.15.2.0", {"start": v(-630.53, 326.15) * mm, "end": v(-631.46, 324.17) * mm});
            skSolve(sketch);
        }
        {
            var Q0;
            Q0 = qSketchRegion(id + "F17", true);
            extrude(context, id + "F18", {"entities" : qUnion([Q0]), "operationType" : NewBodyOperationType.REMOVE, "endBound" : BoundingType.UP_TO_NEXT, "oppositeDirection" : true, "depth" : 25.4 * mm});
        }
        {
            var Q0;
            Q0=makeQuery(id+"F11.opExtrude","CAP_FACE",FACE,{"disambiguationData":[OSD([sQuery(id+"F10.wireOp",EDGE,"E40.bottom"),sQuery(id+"F10.wireOp",EDGE,"E40.top"),sQuery(id+"F10.wireOp",EDGE,"E40.left"),sQuery(id+"F10.wireOp",EDGE,"E40.right"),sQuery(id+"F10.wireOp",EDGE,"E41"),sQuery(id+"F10.wireOp",EDGE,"E42"),sQuery(id+"F10.wireOp",EDGE,"E43"),sQuery(id+"F10.wireOp",EDGE,"E44"),sQuery(id+"F10.wireOp",EDGE,"E45"),sQuery(id+"F10.wireOp",EDGE,"E46"),sQuery(id+"F10.wireOp",EDGE,"E48"),sQuery(id+"F10.wireOp",EDGE,"E49"),sQuery(id+"F10.wireOp",EDGE,"E50")])],"isStart":true});
            cPlane(context, id + "F19", {"entities" : qUnion([Q0]), "cplaneType" : CPlaneType.OFFSET, "offset" : 0 * mm, "width" : 152.4 * mm, "height" : 152.4 * mm});
        }
        {
            var Q0;
            Q0=qCreatedBy(id+"F19.planeOp",FACE);
            var sketch = newSketch(context, id + "F20", { "sketchPlane" : qUnion([Q0])});
            skLineSegment(sketch, "E78.bottom", {"start": v(-377.51, -192.38) * mm, "end": v(-263.21, -192.38) * mm});
            skLineSegment(sketch, "E78.top", {"start": v(-377.51, -351.13) * mm, "end": v(-263.21, -351.13) * mm});
            skLineSegment(sketch, "E78.left", {"start": v(-377.51, -192.38) * mm, "end": v(-377.51, -351.13) * mm});
            skLineSegment(sketch, "E78.right", {"start": v(-263.21, -192.38) * mm, "end": v(-263.21, -351.13) * mm});
            skLineSegment(sketch, "E79", {"start": v(-320.36, -351.13) * mm, "end": v(-320.36, -192.38) * mm, "construction": true});
            skLineSegment(sketch, "E80.bottom", {"start": v(-377.51, -332.08) * mm, "end": v(-390.21, -332.08) * mm});
            skLineSegment(sketch, "E80.top", {"start": v(-377.51, -313.03) * mm, "end": v(-390.21, -313.03) * mm});
            skLineSegment(sketch, "E80.left", {"start": v(-377.51, -332.08) * mm, "end": v(-377.51, -313.03) * mm});
            skLineSegment(sketch, "E80.right", {"start": v(-390.21, -332.08) * mm, "end": v(-390.21, -313.03) * mm});
            skLineSegment(sketch, "E81.1.0.0", {"start": v(-377.51, -293.98) * mm, "end": v(-390.21, -293.98) * mm});
            skLineSegment(sketch, "E81.1.0.1", {"start": v(-390.21, -293.98) * mm, "end": v(-390.21, -274.93) * mm});
            skLineSegment(sketch, "E81.1.0.2", {"start": v(-377.51, -274.93) * mm, "end": v(-390.21, -274.93) * mm});
            skLineSegment(sketch, "E81.2.0.0", {"start": v(-377.51, -255.88) * mm, "end": v(-390.21, -255.88) * mm});
            skLineSegment(sketch, "E81.2.0.1", {"start": v(-390.21, -255.88) * mm, "end": v(-390.21, -236.83) * mm});
            skLineSegment(sketch, "E81.2.0.2", {"start": v(-377.51, -236.83) * mm, "end": v(-390.21, -236.83) * mm});
            skLineSegment(sketch, "E81.3.0.0", {"start": v(-377.51, -217.78) * mm, "end": v(-390.21, -217.78) * mm});
            skLineSegment(sketch, "E81.3.0.1", {"start": v(-390.21, -217.78) * mm, "end": v(-390.21, -198.73) * mm});
            skLineSegment(sketch, "E81.3.0.2", {"start": v(-377.51, -198.73) * mm, "end": v(-390.21, -198.73) * mm});
            skLineSegment(sketch, "E81.direction1", {"start": v(-390.21, -332.08) * mm, "end": v(-390.21, -293.98) * mm, "construction": true});
            skLineSegment(sketch, "E82.MirrorCS", {"start": v(-250.51, -293.98) * mm, "end": v(-250.51, -274.93) * mm});
            skLineSegment(sketch, "E83.MirrorCS", {"start": v(-250.51, -217.78) * mm, "end": v(-250.51, -198.73) * mm});
            skLineSegment(sketch, "E84.MirrorCS", {"start": v(-250.51, -255.88) * mm, "end": v(-250.51, -236.83) * mm});
            skLineSegment(sketch, "E85.MirrorCS", {"start": v(-250.51, -332.08) * mm, "end": v(-250.51, -293.98) * mm, "construction": true});
            skLineSegment(sketch, "E86.MirrorCS", {"start": v(-250.51, -332.08) * mm, "end": v(-250.51, -313.03) * mm});
            skLineSegment(sketch, "E87.MirrorCS", {"start": v(-263.21, -332.08) * mm, "end": v(-250.51, -332.08) * mm});
            skLineSegment(sketch, "E88.MirrorCS", {"start": v(-263.21, -313.03) * mm, "end": v(-250.51, -313.03) * mm});
            skLineSegment(sketch, "E89.MirrorCS", {"start": v(-263.21, -293.98) * mm, "end": v(-250.51, -293.98) * mm});
            skLineSegment(sketch, "E90.MirrorCS", {"start": v(-263.21, -274.93) * mm, "end": v(-250.51, -274.93) * mm});
            skLineSegment(sketch, "E91.MirrorCS", {"start": v(-263.21, -255.88) * mm, "end": v(-250.51, -255.88) * mm});
            skLineSegment(sketch, "E92.MirrorCS", {"start": v(-263.21, -236.83) * mm, "end": v(-250.51, -236.83) * mm});
            skLineSegment(sketch, "E93.MirrorCS", {"start": v(-263.21, -217.78) * mm, "end": v(-250.51, -217.78) * mm});
            skLineSegment(sketch, "E94.MirrorCS", {"start": v(-263.21, -198.73) * mm, "end": v(-250.51, -198.73) * mm});
            skCircle(sketch, "E95", {"center": v(-320.36, -319.38) * mm, "radius": 4.76 * mm});
            skCircle(sketch, "E96", {"center": v(-357.2, -319.38) * mm, "radius": 4.76 * mm});
            skCircle(sketch, "E97.MirrorC", {"center": v(-283.53, -319.38) * mm, "radius": 4.76 * mm});
            skCircle(sketch, "E98", {"center": v(-320.36, -338.43) * mm, "radius": 1.9 * mm});
            skCircle(sketch, "E99", {"center": v(-275.91, -338.43) * mm, "radius": 1.9 * mm});
            skCircle(sketch, "E100", {"center": v(-320.36, -247.81) * mm, "radius": 1.9 * mm});
            skCircle(sketch, "E101", {"center": v(-275.91, -247.81) * mm, "radius": 1.9 * mm});
            skCircle(sketch, "E102.MirrorC", {"center": v(-364.81, -338.43) * mm, "radius": 1.9 * mm});
            skCircle(sketch, "E103.MirrorC", {"center": v(-364.81, -247.81) * mm, "radius": 1.9 * mm});
            skLineSegment(sketch, "E104", {"start": v(-377.51, -224) * mm, "end": v(-263.21, -224) * mm});
            skLineSegment(sketch, "E105", {"start": v(-371.16, -224) * mm, "end": v(-371.16, -226.18) * mm});
            skLineSegment(sketch, "E106", {"start": v(-371.16, -226.18) * mm, "end": v(-354.02, -226.18) * mm});
            skLineSegment(sketch, "E107", {"start": v(-354.02, -226.18) * mm, "end": v(-354.02, -224) * mm});
            skLineSegment(sketch, "E108.MirrorCS", {"start": v(-354.02, -221.82) * mm, "end": v(-354.02, -224) * mm});
            skLineSegment(sketch, "E109.MirrorCS", {"start": v(-371.16, -221.82) * mm, "end": v(-354.02, -221.82) * mm});
            skLineSegment(sketch, "E110.MirrorCS", {"start": v(-371.16, -224) * mm, "end": v(-371.16, -221.82) * mm});
            skLineSegment(sketch, "E111.1.0.0", {"start": v(-325.44, -226.18) * mm, "end": v(-325.44, -224) * mm});
            skLineSegment(sketch, "E111.1.0.1", {"start": v(-342.59, -226.18) * mm, "end": v(-325.44, -226.18) * mm});
            skLineSegment(sketch, "E111.1.0.2", {"start": v(-342.59, -224) * mm, "end": v(-342.59, -226.18) * mm});
            skLineSegment(sketch, "E111.1.0.3", {"start": v(-342.59, -224) * mm, "end": v(-342.59, -221.82) * mm});
            skLineSegment(sketch, "E111.1.0.4", {"start": v(-342.59, -221.82) * mm, "end": v(-325.44, -221.82) * mm});
            skLineSegment(sketch, "E111.1.0.5", {"start": v(-325.44, -221.82) * mm, "end": v(-325.44, -224) * mm});
            skLineSegment(sketch, "E111.2.0.0", {"start": v(-296.87, -226.18) * mm, "end": v(-296.87, -224) * mm});
            skLineSegment(sketch, "E111.2.0.1", {"start": v(-314.01, -226.18) * mm, "end": v(-296.87, -226.18) * mm});
            skLineSegment(sketch, "E111.2.0.2", {"start": v(-314.01, -224) * mm, "end": v(-314.01, -226.18) * mm});
            skLineSegment(sketch, "E111.2.0.3", {"start": v(-314.01, -224) * mm, "end": v(-314.01, -221.82) * mm});
            skLineSegment(sketch, "E111.2.0.4", {"start": v(-314.01, -221.82) * mm, "end": v(-296.87, -221.82) * mm});
            skLineSegment(sketch, "E111.2.0.5", {"start": v(-296.87, -221.82) * mm, "end": v(-296.87, -224) * mm});
            skLineSegment(sketch, "E111.3.0.0", {"start": v(-268.3, -226.18) * mm, "end": v(-268.3, -224) * mm});
            skLineSegment(sketch, "E111.3.0.1", {"start": v(-285.44, -226.18) * mm, "end": v(-268.3, -226.18) * mm});
            skLineSegment(sketch, "E111.3.0.2", {"start": v(-285.44, -224) * mm, "end": v(-285.44, -226.18) * mm});
            skLineSegment(sketch, "E111.3.0.3", {"start": v(-285.44, -224) * mm, "end": v(-285.44, -221.82) * mm});
            skLineSegment(sketch, "E111.3.0.4", {"start": v(-285.44, -221.82) * mm, "end": v(-268.3, -221.82) * mm});
            skLineSegment(sketch, "E111.3.0.5", {"start": v(-268.3, -221.82) * mm, "end": v(-268.3, -224) * mm});
            skLineSegment(sketch, "E111.direction1", {"start": v(-354.02, -226.18) * mm, "end": v(-325.44, -226.18) * mm, "construction": true});
            skSolve(sketch);
        }
        {
            var Q0;
            Q0 = qSketchRegion(id + "F20", true);
            extrude(context, id + "F21", {"entities" : qUnion([Q0]), "depth" : 4.37 * mm});
        }
        {
            var Q0;
            Q0=qCreatedBy(id+"F19.planeOp",FACE);
            var sketch = newSketch(context, id + "F22", { "sketchPlane" : qUnion([Q0])});
            skLineSegment(sketch, "E112.bottom", {"start": v(-407.34, -105.94) * mm, "end": v(-293.04, -105.94) * mm});
            skLineSegment(sketch, "E112.top", {"start": v(-407.34, -18.94) * mm, "end": v(-293.04, -18.94) * mm});
            skLineSegment(sketch, "E112.left", {"start": v(-407.34, -105.94) * mm, "end": v(-407.34, -18.94) * mm});
            skLineSegment(sketch, "E112.right", {"start": v(-293.04, -105.94) * mm, "end": v(-293.04, -18.94) * mm});
            skLineSegment(sketch, "E113.bottom", {"start": v(-407.34, -82.44) * mm, "end": v(-420.04, -82.44) * mm});
            skLineSegment(sketch, "E113.top", {"start": v(-407.34, -99.59) * mm, "end": v(-420.04, -99.59) * mm});
            skLineSegment(sketch, "E113.left", {"start": v(-407.34, -82.44) * mm, "end": v(-407.34, -99.59) * mm});
            skLineSegment(sketch, "E113.right", {"start": v(-420.04, -82.44) * mm, "end": v(-420.04, -99.59) * mm});
            skLineSegment(sketch, "E114.0.1.0", {"start": v(-407.34, -71.01) * mm, "end": v(-420.04, -71.01) * mm});
            skLineSegment(sketch, "E114.0.1.1", {"start": v(-407.34, -53.87) * mm, "end": v(-420.04, -53.87) * mm});
            skLineSegment(sketch, "E114.0.1.2", {"start": v(-420.04, -53.87) * mm, "end": v(-420.04, -71.01) * mm});
            skLineSegment(sketch, "E114.0.2.0", {"start": v(-407.34, -42.44) * mm, "end": v(-420.04, -42.44) * mm});
            skLineSegment(sketch, "E114.0.2.1", {"start": v(-407.34, -25.3) * mm, "end": v(-420.04, -25.3) * mm});
            skLineSegment(sketch, "E114.0.2.2", {"start": v(-420.04, -25.3) * mm, "end": v(-420.04, -42.44) * mm});
            skLineSegment(sketch, "E114.direction1", {"start": v(-420.04, -99.59) * mm, "end": v(-360.9, -108.1) * mm, "construction": true});
            skLineSegment(sketch, "E114.direction2", {"start": v(-420.04, -99.59) * mm, "end": v(-420.04, -71.01) * mm, "construction": true});
            skLineSegment(sketch, "E115", {"start": v(-350.2, -105.94) * mm, "end": v(-350.2, -18.94) * mm, "construction": true});
            skLineSegment(sketch, "E116.MirrorCS", {"start": v(-280.34, -82.44) * mm, "end": v(-280.34, -99.59) * mm});
            skLineSegment(sketch, "E117.MirrorCS", {"start": v(-280.34, -53.87) * mm, "end": v(-280.34, -71.01) * mm});
            skLineSegment(sketch, "E118.MirrorCS", {"start": v(-280.34, -99.59) * mm, "end": v(-280.34, -71.01) * mm, "construction": true});
            skLineSegment(sketch, "E119.MirrorCS", {"start": v(-280.34, -25.3) * mm, "end": v(-280.34, -42.44) * mm});
            skLineSegment(sketch, "E120.MirrorCS", {"start": v(-293.04, -82.44) * mm, "end": v(-280.34, -82.44) * mm});
            skLineSegment(sketch, "E121.MirrorCS", {"start": v(-293.04, -99.59) * mm, "end": v(-280.34, -99.59) * mm});
            skLineSegment(sketch, "E122.MirrorCS", {"start": v(-293.04, -71.01) * mm, "end": v(-280.34, -71.01) * mm});
            skLineSegment(sketch, "E123.MirrorCS", {"start": v(-293.04, -53.87) * mm, "end": v(-280.34, -53.87) * mm});
            skLineSegment(sketch, "E124.MirrorCS", {"start": v(-293.04, -42.44) * mm, "end": v(-280.34, -42.44) * mm});
            skLineSegment(sketch, "E125.MirrorCS", {"start": v(-293.04, -25.3) * mm, "end": v(-280.34, -25.3) * mm});
            skLineSegment(sketch, "E126.bottom", {"start": v(-401, -18.94) * mm, "end": v(-383.85, -18.94) * mm});
            skLineSegment(sketch, "E126.top", {"start": v(-401, -15.77) * mm, "end": v(-383.85, -15.77) * mm});
            skLineSegment(sketch, "E126.left", {"start": v(-401, -18.94) * mm, "end": v(-401, -15.77) * mm});
            skLineSegment(sketch, "E126.right", {"start": v(-383.85, -18.94) * mm, "end": v(-383.85, -15.77) * mm});
            skLineSegment(sketch, "E127.1.0.0", {"start": v(-355.27, -18.94) * mm, "end": v(-355.27, -15.77) * mm});
            skLineSegment(sketch, "E127.1.0.1", {"start": v(-372.42, -15.77) * mm, "end": v(-355.27, -15.77) * mm});
            skLineSegment(sketch, "E127.1.0.2", {"start": v(-372.42, -18.94) * mm, "end": v(-372.42, -15.77) * mm});
            skLineSegment(sketch, "E127.2.0.0", {"start": v(-326.7, -18.94) * mm, "end": v(-326.7, -15.77) * mm});
            skLineSegment(sketch, "E127.2.0.1", {"start": v(-343.84, -15.77) * mm, "end": v(-326.7, -15.77) * mm});
            skLineSegment(sketch, "E127.2.0.2", {"start": v(-343.84, -18.94) * mm, "end": v(-343.84, -15.77) * mm});
            skLineSegment(sketch, "E127.3.0.0", {"start": v(-298.12, -18.94) * mm, "end": v(-298.12, -15.77) * mm});
            skLineSegment(sketch, "E127.3.0.1", {"start": v(-315.27, -15.77) * mm, "end": v(-298.12, -15.77) * mm});
            skLineSegment(sketch, "E127.3.0.2", {"start": v(-315.27, -18.94) * mm, "end": v(-315.27, -15.77) * mm});
            skLineSegment(sketch, "E127.direction1", {"start": v(-383.85, -18.94) * mm, "end": v(-355.27, -18.94) * mm, "construction": true});
            skSolve(sketch);
        }
        {
            var Q0;
            Q0 = qSketchRegion(id + "F22", true);
            extrude(context, id + "F23", {"entities" : qUnion([Q0]), "depth" : 4.37 * mm});
        }
        {
            var Q0;
            Q0=qCreatedBy(id+"F19.planeOp",FACE);
            var sketch = newSketch(context, id + "F24", { "sketchPlane" : qUnion([Q0])});
            skLineSegment(sketch, "E128.bottom", {"start": v(-186.1, -361.67) * mm, "end": v(-71.8, -361.67) * mm});
            skLineSegment(sketch, "E128.top", {"start": v(-186.1, -239.3) * mm, "end": v(-71.8, -239.3) * mm});
            skLineSegment(sketch, "E128.left", {"start": v(-186.1, -361.67) * mm, "end": v(-186.1, -239.3) * mm});
            skLineSegment(sketch, "E128.right", {"start": v(-71.8, -361.67) * mm, "end": v(-71.8, -239.3) * mm});
            skLineSegment(sketch, "E129", {"start": v(-128.94, -361.67) * mm, "end": v(-128.94, -239.3) * mm, "construction": true});
            skCircle(sketch, "E130", {"center": v(-128.94, -348.97) * mm, "radius": 1.9 * mm});
            skCircle(sketch, "E131", {"center": v(-173.4, -348.97) * mm, "radius": 1.9 * mm});
            skCircle(sketch, "E132", {"center": v(-128.94, -258.36) * mm, "radius": 1.9 * mm});
            skCircle(sketch, "E133", {"center": v(-173.4, -258.36) * mm, "radius": 1.9 * mm});
            skCircle(sketch, "E134", {"center": v(-128.94, -329.92) * mm, "radius": 1.9 * mm});
            skCircle(sketch, "E135", {"center": v(-165.77, -329.92) * mm, "radius": 1.9 * mm});
            skCircle(sketch, "E136.MirrorC", {"center": v(-84.5, -348.97) * mm, "radius": 1.9 * mm});
            skCircle(sketch, "E137.MirrorC", {"center": v(-92.11, -329.92) * mm, "radius": 1.9 * mm});
            skCircle(sketch, "E138.MirrorC", {"center": v(-84.5, -258.36) * mm, "radius": 1.9 * mm});
            skSolve(sketch);
        }
        {
            var Q0;
            Q0=makeQuery(id+"F24.imprint","IMPRINT",FACE,{"disambiguationData":[TD([[makeQuery(id+"F24.imprint","IMPRINT",EDGE,{"derivedFrom":sQuery(id+"F24.wireOp",EDGE,"E128.bottom")}),1.0]])]});
            extrude(context, id + "F25", {"entities" : qUnion([Q0]), "depth" : 4.76 * mm});
        }
        {
            var Q0;
            Q0=qCreatedBy(makeId("Top.planeOp"),FACE);
            var sketch = newSketch(context, id + "F26", { "sketchPlane" : qUnion([Q0])});
            skLineSegment(sketch, "E139.bottom", {"start": v(-311.4, 539.7) * mm, "end": v(-11.36, 539.7) * mm});
            skLineSegment(sketch, "E139.top", {"start": v(-311.4, 492.07) * mm, "end": v(-11.36, 492.07) * mm});
            skLineSegment(sketch, "E139.left", {"start": v(-311.4, 539.7) * mm, "end": v(-311.4, 492.07) * mm});
            skLineSegment(sketch, "E139.right", {"start": v(-11.36, 539.7) * mm, "end": v(-11.36, 492.07) * mm});
            skCircle(sketch, "E140", {"center": v(-263.78, 515.88) * mm, "radius": 1.9 * mm});
            skPoint(sketch, "E140.centerSnap0", {"position": v(-311.4, 515.88) * mm});
            skCircle(sketch, "E141", {"center": v(-190.12, 515.88) * mm, "radius": 1.9 * mm});
            skCircle(sketch, "E142", {"center": v(-226.95, 515.88) * mm, "radius": 1.9 * mm});
            skSolve(sketch);
        }
        {
            var Q0;
            Q0=makeQuery(id+"F26.imprint","IMPRINT",FACE,{"disambiguationData":[TD([[makeQuery(id+"F26.imprint","IMPRINT",EDGE,{"derivedFrom":sQuery(id+"F26.wireOp",EDGE,"E139.bottom")}),-1.0]])]});
            extrude(context, id + "F27", {"entities" : qUnion([Q0]), "depth" : 12.7 * mm});
        }
        {
            var Q0;
            Q0=qCreatedBy(id+"F19.planeOp",FACE);
            var sketch = newSketch(context, id + "F28", { "sketchPlane" : qUnion([Q0])});
            skLineSegment(sketch, "E143.bottom", {"start": v(-510.8, -742.33) * mm, "end": v(-79, -742.33) * mm});
            skLineSegment(sketch, "E143.top", {"start": v(-510.8, -648.98) * mm, "end": v(-79, -648.98) * mm});
            skLineSegment(sketch, "E143.left", {"start": v(-510.8, -742.33) * mm, "end": v(-510.8, -648.98) * mm});
            skLineSegment(sketch, "E143.right", {"start": v(-79, -742.33) * mm, "end": v(-79, -648.98) * mm});
            skCircle(sketch, "E144", {"center": v(-333, -695.66) * mm, "radius": 1.9 * mm});
            skPoint(sketch, "E144.centerSnap0", {"position": v(-510.8, -695.66) * mm});
            skCircle(sketch, "E145", {"center": v(-294.9, -695.66) * mm, "radius": 1.9 * mm});
            skPoint(sketch, "E145.centerSnap0", {"position": v(-294.9, -742.33) * mm});
            skCircle(sketch, "E146", {"center": v(-256.8, -695.66) * mm, "radius": 1.9 * mm});
            skSolve(sketch);
        }
        {
            var Q0;
            Q0=makeQuery(id+"F28.imprint","IMPRINT",FACE,{"disambiguationData":[TD([[makeQuery(id+"F28.imprint","IMPRINT",EDGE,{"derivedFrom":sQuery(id+"F28.wireOp",EDGE,"E143.bottom")}),1.0]])]});
            extrude(context, id + "F29", {"entities" : qUnion([Q0]), "depth" : 4.76 * mm});
        }
        {
            var Q0;
            Q0=makeQuery(id+"F29.opExtrude","CAP_FACE",FACE,{"disambiguationData":[OSD([sQuery(id+"F28.wireOp",EDGE,"E143.bottom"),sQuery(id+"F28.wireOp",EDGE,"E143.top"),sQuery(id+"F28.wireOp",EDGE,"E143.left"),sQuery(id+"F28.wireOp",EDGE,"E143.right")])],"isStart":true});
            var sketch = newSketch(context, id + "F30", { "sketchPlane" : qUnion([Q0])});
            skLineSegment(sketch, "E147.bottom", {"start": v(-510.8, 742.33) * mm, "end": v(-79, 742.33) * mm});
            skLineSegment(sketch, "E147.top", {"start": v(-510.8, 737.57) * mm, "end": v(-79, 737.57) * mm});
            skLineSegment(sketch, "E147.left", {"start": v(-510.8, 742.33) * mm, "end": v(-510.8, 737.57) * mm});
            skLineSegment(sketch, "E147.right", {"start": v(-79, 742.33) * mm, "end": v(-79, 737.57) * mm});
            skLineSegment(sketch, "E148.bottom", {"start": v(-510.8, 648.98) * mm, "end": v(-79, 648.98) * mm});
            skLineSegment(sketch, "E148.top", {"start": v(-510.8, 653.75) * mm, "end": v(-79, 653.75) * mm});
            skLineSegment(sketch, "E148.left", {"start": v(-510.8, 648.98) * mm, "end": v(-510.8, 653.75) * mm});
            skLineSegment(sketch, "E148.right", {"start": v(-79, 648.98) * mm, "end": v(-79, 653.75) * mm});
            skSolve(sketch);
        }
        {
            var Q0;
            Q0=makeQuery(id+"F30.imprint","IMPRINT",FACE,{"disambiguationData":[TD([[makeQuery(id+"F30.imprint","IMPRINT",EDGE,{"derivedFrom":sQuery(id+"F30.wireOp",EDGE,"E147.bottom")}),-1.0]])]});
            extrude(context, id + "F31", {"entities" : qUnion([Q0]), "operationType" : NewBodyOperationType.ADD, "depth" : 152.4 * mm});
        }
        {
            var Q0;
            Q0=makeQuery(id+"F29.opExtrude","CAP_FACE",FACE,{"disambiguationData":[OSD([sQuery(id+"F28.wireOp",EDGE,"E143.bottom"),sQuery(id+"F28.wireOp",EDGE,"E143.top"),sQuery(id+"F28.wireOp",EDGE,"E143.left"),sQuery(id+"F28.wireOp",EDGE,"E143.right")])],"isStart":true});
            var sketch = newSketch(context, id + "F32", { "sketchPlane" : qUnion([Q0])});
            skLineSegment(sketch, "E149.bottom", {"start": v(-510.8, 648.98) * mm, "end": v(-79, 648.98) * mm});
            skLineSegment(sketch, "E149.top", {"start": v(-510.8, 653.75) * mm, "end": v(-79, 653.75) * mm});
            skLineSegment(sketch, "E149.left", {"start": v(-510.8, 648.98) * mm, "end": v(-510.8, 653.75) * mm});
            skLineSegment(sketch, "E149.right", {"start": v(-79, 648.98) * mm, "end": v(-79, 653.75) * mm});
            skSolve(sketch);
        }
        {
            var Q0;
            Q0=makeQuery(id+"F32.imprint","IMPRINT",FACE,{"disambiguationData":[TD([[makeQuery(id+"F32.imprint","IMPRINT",EDGE,{"derivedFrom":sQuery(id+"F32.wireOp",EDGE,"E149.bottom")}),1.0]])]});
            extrude(context, id + "F33", {"entities" : qUnion([Q0]), "operationType" : NewBodyOperationType.ADD, "depth" : 82.55 * mm});
        }
        {
            var Q0;
            Q0=qCreatedBy(makeId("Top.planeOp"),FACE);
            var sketch = newSketch(context, id + "F34", { "sketchPlane" : qUnion([Q0])});
            skLineSegment(sketch, "E150.bottom", {"start": v(0, 0) * mm, "end": v(406.4, 0) * mm});
            skLineSegment(sketch, "E150.top", {"start": v(0, 76.2) * mm, "end": v(406.4, 76.2) * mm});
            skLineSegment(sketch, "E150.left", {"start": v(0, 0) * mm, "end": v(0, 76.2) * mm});
            skLineSegment(sketch, "E150.right", {"start": v(406.4, 0) * mm, "end": v(406.4, 76.2) * mm});
            skSolve(sketch);
        }
        {
            var Q0;
            Q0=makeQuery(id+"F34.imprint","IMPRINT",FACE,{"disambiguationData":[TD([[makeQuery(id+"F34.imprint","IMPRINT",EDGE,{"derivedFrom":sQuery(id+"F34.wireOp",EDGE,"E150.bottom")}),1.0]])]});
            extrude(context, id + "F35", {"entities" : qUnion([Q0]), "depth" : 51.43 * mm});
        }
        {
            var Q0;
            Q0=makeQuery(id+"F35.opExtrude","SWEPT_FACE",FACE,{"disambiguationData":[OSD([sQuery(id+"F34.wireOp",EDGE,"E150.bottom")])]});
            var sketch = newSketch(context, id + "F36", { "sketchPlane" : qUnion([Q0])});
            skCircle(sketch, "E151", {"center": v(16.51, 16.51) * mm, "radius": 12.7 * mm});
            skCircle(sketch, "E152", {"center": v(16.51, 26.29) * mm, "radius": 1.9 * mm});
            skCircle(sketch, "E153", {"center": v(16.51, 16.51) * mm, "radius": 3.97 * mm});
            skCircle(sketch, "E154", {"center": v(16.51, 16.51) * mm, "radius": 9.78 * mm, "construction": true});
            skCircle(sketch, "E155.1.0", {"center": v(9.6, 23.42) * mm, "radius": 1.9 * mm});
            skCircle(sketch, "E155.2.0", {"center": v(6.73, 16.51) * mm, "radius": 1.9 * mm});
            skCircle(sketch, "E155.3.0", {"center": v(9.6, 9.6) * mm, "radius": 1.9 * mm});
            skLineSegment(sketch, "E156", {"start": v(33.02, 48.26) * mm, "end": v(406.4, 48.26) * mm});
            skLineSegment(sketch, "E157", {"start": v(33.02, 0) * mm, "end": v(33.02, 48.26) * mm});
            skCircle(sketch, "E158.1.4.0", {"center": v(16.51, 6.73) * mm, "radius": 1.9 * mm});
            skCircle(sketch, "E158.1.5.0", {"center": v(23.42, 9.6) * mm, "radius": 1.9 * mm});
            skCircle(sketch, "E158.1.6.0", {"center": v(26.29, 16.51) * mm, "radius": 1.9 * mm});
            skCircle(sketch, "E158.1.7.0", {"center": v(23.42, 23.42) * mm, "radius": 1.9 * mm});
            skCircle(sketch, "E159", {"center": v(16.51, 16.51) * mm, "radius": 16.51 * mm});
            skSolve(sketch);
        }
        {
            var Q0;
            {var subQ5=sQuery(id+"F36.wireOp",EDGE,"E156");Q0=makeQuery(id+"F36.imprint","IMPRINT",FACE,{"disambiguationData":[TD([[makeQuery(id+"F36.imprint","IMPRINT",EDGE,{"derivedFrom":subQ5}),-1.0]])]});}
            var Q1;
            Q1=makeQuery(id+"F36.imprint","IMPRINT",FACE,{"disambiguationData":[TD([[makeQuery(id+"F36.imprint","IMPRINT",EDGE,{"derivedFrom":sQuery(id+"F36.wireOp",EDGE,"E158.1.7.0")}),1.0]])]});
            var Q2;
            Q2=makeQuery(id+"F36.imprint","IMPRINT",FACE,{"disambiguationData":[TD([[makeQuery(id+"F36.imprint","IMPRINT",EDGE,{"derivedFrom":sQuery(id+"F36.wireOp",EDGE,"E152")}),1.0]])]});
            var Q3;
            Q3=makeQuery(id+"F36.imprint","IMPRINT",FACE,{"disambiguationData":[TD([[makeQuery(id+"F36.imprint","IMPRINT",EDGE,{"derivedFrom":sQuery(id+"F36.wireOp",EDGE,"E155.1.0")}),1.0]])]});
            var Q4;
            Q4=makeQuery(id+"F36.imprint","IMPRINT",FACE,{"disambiguationData":[TD([[makeQuery(id+"F36.imprint","IMPRINT",EDGE,{"derivedFrom":sQuery(id+"F36.wireOp",EDGE,"E155.2.0")}),1.0]])]});
            var Q5;
            Q5=makeQuery(id+"F36.imprint","IMPRINT",FACE,{"disambiguationData":[TD([[makeQuery(id+"F36.imprint","IMPRINT",EDGE,{"derivedFrom":sQuery(id+"F36.wireOp",EDGE,"E155.3.0")}),1.0]])]});
            var Q6;
            Q6=makeQuery(id+"F36.imprint","IMPRINT",FACE,{"disambiguationData":[TD([[makeQuery(id+"F36.imprint","IMPRINT",EDGE,{"derivedFrom":sQuery(id+"F36.wireOp",EDGE,"E158.1.4.0")}),1.0]])]});
            var Q7;
            Q7=makeQuery(id+"F36.imprint","IMPRINT",FACE,{"disambiguationData":[TD([[makeQuery(id+"F36.imprint","IMPRINT",EDGE,{"derivedFrom":sQuery(id+"F36.wireOp",EDGE,"E158.1.5.0")}),1.0]])]});
            var Q8;
            Q8=makeQuery(id+"F36.imprint","IMPRINT",FACE,{"disambiguationData":[TD([[makeQuery(id+"F36.imprint","IMPRINT",EDGE,{"derivedFrom":sQuery(id+"F36.wireOp",EDGE,"E158.1.6.0")}),1.0]])]});
            var Q9;
            Q9=makeQuery(id+"F36.imprint","IMPRINT",FACE,{"disambiguationData":[TD([[makeQuery(id+"F36.imprint","IMPRINT",EDGE,{"derivedFrom":sQuery(id+"F36.wireOp",EDGE,"E153")}),1.0]])]});
            var Q10;
            {var subQ0=sQuery(id+"F36.wireOp",EDGE,"E157");var subQ1=makeQuery(id+"F35.opExtrude","CAP_EDGE",EDGE,{"disambiguationData":[OSD([sQuery(id+"F34.wireOp",EDGE,"E150.bottom")])],"isStart":true});var subQ2=makeQuery(id+"F36.imprint","INTERSECT",VERTEX,{"derivedFrom":[subQ1,subQ0]});Q10=makeQuery(id+"F36.imprint","IMPRINT",FACE,{"disambiguationData":[TD([[makeQuery(id+"F36.imprint","IMPRINT",EDGE,{"disambiguationData":[TD([[subQ2,-1.0]])],"derivedFrom":subQ0}),1.0]])]});}
            var Q11;
            {var subQ0=sQuery(id+"F36.wireOp",EDGE,"E159");var subQ1=sQuery(id+"F34.wireOp",EDGE,"E150.bottom");var subQ4=makeQuery(id+"F35.opExtrude","CAP_EDGE",EDGE,{"disambiguationData":[OSD([subQ1])],"isStart":true});var subQ5=makeQuery(id+"F36.imprint","INTERSECT",VERTEX,{"derivedFrom":[subQ4,subQ0]});Q11=makeQuery(id+"F36.imprint","IMPRINT",FACE,{"disambiguationData":[TD([[makeQuery(id+"F36.imprint","IMPRINT",EDGE,{"disambiguationData":[TD([[subQ5,1.0]])],"derivedFrom":subQ0}),-1.0]])]});}
            extrude(context, id + "F37", {"entities" : qUnion([Q0, Q1, Q2, Q3, Q4, Q5, Q6, Q7, Q8, Q9, Q10, Q11]), "operationType" : NewBodyOperationType.REMOVE, "endBound" : BoundingType.UP_TO_NEXT, "oppositeDirection" : true, "depth" : 25.4 * mm});
        }
        {
            var Q0;
            Q0=makeQuery(id+"F35.opExtrude","SWEPT_FACE",FACE,{"disambiguationData":[OSD([sQuery(id+"F34.wireOp",EDGE,"E150.left")])]});
            var sketch = newSketch(context, id + "F38", { "sketchPlane" : qUnion([Q0])});
            skLineSegment(sketch, "E160.bottom", {"start": v(-73.02, 48.26) * mm, "end": v(-3.18, 48.26) * mm});
            skLineSegment(sketch, "E160.top", {"start": v(-73.02, 0) * mm, "end": v(-3.18, 0) * mm});
            skLineSegment(sketch, "E160.left", {"start": v(-73.02, 48.26) * mm, "end": v(-73.02, 0) * mm});
            skLineSegment(sketch, "E160.right", {"start": v(-3.18, 48.26) * mm, "end": v(-3.18, 0) * mm});
            skSolve(sketch);
        }
        {
            var Q0;
            {var subQ0=sQuery(id+"F38.wireOp",EDGE,"E160.top");Q0=makeQuery(id+"F38.imprint","IMPRINT",FACE,{"disambiguationData":[TD([[makeQuery(id+"F38.imprint","IMPRINT",EDGE,{"derivedFrom":subQ0}),1.0]])]});}
            var Q1;
            {var subQ0=sQuery(id+"F38.wireOp",EDGE,"E160.bottom");Q1=makeQuery(id+"F38.imprint","IMPRINT",FACE,{"disambiguationData":[TD([[makeQuery(id+"F38.imprint","IMPRINT",EDGE,{"derivedFrom":subQ0}),-1.0]])]});}
            extrude(context, id + "F39", {"entities" : qUnion([Q0, Q1]), "operationType" : NewBodyOperationType.REMOVE, "endBound" : BoundingType.THROUGH_ALL, "oppositeDirection" : true, "depth" : 25.4 * mm});
        }
        {
            var Q0;
            Q0=makeQuery(id+"F29.opExtrude","CAP_FACE",FACE,{"disambiguationData":[OSD([sQuery(id+"F28.wireOp",EDGE,"E143.bottom"),sQuery(id+"F28.wireOp",EDGE,"E143.top"),sQuery(id+"F28.wireOp",EDGE,"E143.left"),sQuery(id+"F28.wireOp",EDGE,"E143.right"),sQuery(id+"F28.wireOp",EDGE,"E144"),sQuery(id+"F28.wireOp",EDGE,"E145"),sQuery(id+"F28.wireOp",EDGE,"E146")])],"isStart":true});
            var sketch = newSketch(context, id + "F40", { "sketchPlane" : qUnion([Q0])});
            skLineSegment(sketch, "E161.bottom", {"start": v(-510.8, 737.57) * mm, "end": v(-460, 737.57) * mm});
            skLineSegment(sketch, "E161.top", {"start": v(-510.8, 731.22) * mm, "end": v(-460, 731.22) * mm});
            skLineSegment(sketch, "E161.left", {"start": v(-510.8, 737.57) * mm, "end": v(-510.8, 731.22) * mm});
            skLineSegment(sketch, "E161.right", {"start": v(-460, 737.57) * mm, "end": v(-460, 731.22) * mm});
            skLineSegment(sketch, "E162.bottom", {"start": v(-510.8, 661.68) * mm, "end": v(-460, 661.68) * mm});
            skLineSegment(sketch, "E162.top", {"start": v(-510.8, 653.75) * mm, "end": v(-460, 653.75) * mm});
            skLineSegment(sketch, "E162.left", {"start": v(-510.8, 661.68) * mm, "end": v(-510.8, 653.75) * mm});
            skLineSegment(sketch, "E162.right", {"start": v(-460, 661.68) * mm, "end": v(-460, 653.75) * mm});
            skCircle(sketch, "E163", {"center": v(-479.05, 685.5) * mm, "radius": 9.78 * mm, "construction": true});
            skCircle(sketch, "E164", {"center": v(-479.05, 695.28) * mm, "radius": 1.9 * mm});
            skCircle(sketch, "E165.1.0", {"center": v(-488.82, 685.5) * mm, "radius": 1.9 * mm});
            skCircle(sketch, "E165.2.0", {"center": v(-479.05, 675.72) * mm, "radius": 1.9 * mm});
            skCircle(sketch, "E165.3.0", {"center": v(-469.27, 685.5) * mm, "radius": 1.9 * mm});
            skLineSegment(sketch, "E166.bottom", {"start": v(-510.8, 731.22) * mm, "end": v(-498.1, 731.22) * mm});
            skLineSegment(sketch, "E166.top", {"start": v(-510.8, 661.68) * mm, "end": v(-498.1, 661.68) * mm});
            skLineSegment(sketch, "E166.left", {"start": v(-510.8, 731.22) * mm, "end": v(-510.8, 661.68) * mm});
            skLineSegment(sketch, "E166.right", {"start": v(-498.1, 731.22) * mm, "end": v(-498.1, 661.68) * mm});
            skLineSegment(sketch, "E167.top", {"start": v(-510.8, 702.96) * mm, "end": v(-460, 702.96) * mm});
            skLineSegment(sketch, "E167.left", {"start": v(-510.8, 737.57) * mm, "end": v(-510.8, 702.96) * mm});
            skLineSegment(sketch, "E167.right", {"start": v(-460, 737.57) * mm, "end": v(-460, 702.96) * mm});
            skSolve(sketch);
        }
        {
            var Q0;
            Q0=makeQuery(id+"F40.imprint","IMPRINT",FACE,{"disambiguationData":[TD([[makeQuery(id+"F40.imprint","IMPRINT",EDGE,{"derivedFrom":sQuery(id+"F40.wireOp",EDGE,"E161.bottom")}),-1.0]])]});
            var Q1;
            Q1=makeQuery(id+"F40.imprint","IMPRINT",FACE,{"disambiguationData":[TD([[makeQuery(id+"F40.imprint","IMPRINT",EDGE,{"derivedFrom":sQuery(id+"F40.wireOp",EDGE,"E162.bottom")}),-1.0]])]});
            var Q2;
            Q2=makeQuery(id+"F40.imprint","IMPRINT",FACE,{"disambiguationData":[TD([[makeQuery(id+"F40.imprint","IMPRINT",EDGE,{"derivedFrom":sQuery(id+"F40.wireOp",EDGE,"E165.3.0")}),1.0]])]});
            var Q3;
            Q3=makeQuery(id+"F40.imprint","IMPRINT",FACE,{"disambiguationData":[TD([[makeQuery(id+"F40.imprint","IMPRINT",EDGE,{"derivedFrom":sQuery(id+"F40.wireOp",EDGE,"E165.2.0")}),1.0]])]});
            var Q4;
            Q4=makeQuery(id+"F40.imprint","IMPRINT",FACE,{"disambiguationData":[TD([[makeQuery(id+"F40.imprint","IMPRINT",EDGE,{"derivedFrom":sQuery(id+"F40.wireOp",EDGE,"E165.1.0")}),1.0]])]});
            var Q5;
            Q5=makeQuery(id+"F40.imprint","IMPRINT",FACE,{"disambiguationData":[TD([[makeQuery(id+"F40.imprint","IMPRINT",EDGE,{"derivedFrom":sQuery(id+"F40.wireOp",EDGE,"E164")}),1.0]])]});
            var Q6;
            Q6=makeQuery(id+"F40.imprint","IMPRINT",FACE,{"disambiguationData":[TD([[makeQuery(id+"F40.imprint","IMPRINT",EDGE,{"derivedFrom":sQuery(id+"F40.wireOp",EDGE,"E166.bottom")}),-1.0]])]});
            var Q7;
            {var subQ4=sQuery(id+"F40.wireOp",EDGE,"E161.top");Q7=makeQuery(id+"F40.imprint","IMPRINT",FACE,{"disambiguationData":[TD([[makeQuery(id+"F40.imprint","IMPRINT",EDGE,{"derivedFrom":subQ4}),-1.0]])]});}
            var Q8;
            Q8=makeQuery(id+"F40.imprint","IMPRINT",FACE,{"disambiguationData":[TD([[makeQuery(id+"F40.imprint","IMPRINT",EDGE,{"derivedFrom":sQuery(id+"F40.wireOp",EDGE,"E161.top")}),1.0]])]});
            var Q9;
            {var subQ0=sQuery(id+"F40.wireOp",EDGE,"E166.top");Q9=makeQuery(id+"F40.imprint","IMPRINT",FACE,{"disambiguationData":[TD([[makeQuery(id+"F40.imprint","IMPRINT",EDGE,{"derivedFrom":subQ0}),1.0]])]});}
            extrude(context, id + "F41", {"entities" : qUnion([Q0, Q1, Q2, Q3, Q4, Q5, Q6, Q7, Q8, Q9]), "operationType" : NewBodyOperationType.REMOVE, "endBound" : BoundingType.UP_TO_NEXT, "oppositeDirection" : true, "depth" : 25.4 * mm});
        }
        {
            var Q0;
            Q0=makeQuery(id+"F29.opExtrude","CAP_FACE",FACE,{"disambiguationData":[OSD([sQuery(id+"F28.wireOp",EDGE,"E143.bottom"),sQuery(id+"F28.wireOp",EDGE,"E143.top"),sQuery(id+"F28.wireOp",EDGE,"E143.left"),sQuery(id+"F28.wireOp",EDGE,"E143.right"),sQuery(id+"F28.wireOp",EDGE,"E144"),sQuery(id+"F28.wireOp",EDGE,"E145"),sQuery(id+"F28.wireOp",EDGE,"E146")])],"isStart":false});
            var sketch = newSketch(context, id + "F42", { "sketchPlane" : qUnion([Q0])});
            skLineSegment(sketch, "E168.bottom", {"start": v(-498.1, -742.33) * mm, "end": v(-461.01, -742.33) * mm});
            skLineSegment(sketch, "E168.top", {"start": v(-498.1, -737.57) * mm, "end": v(-461.01, -737.57) * mm});
            skLineSegment(sketch, "E168.left", {"start": v(-498.1, -742.33) * mm, "end": v(-498.1, -737.57) * mm});
            skLineSegment(sketch, "E168.right", {"start": v(-461.01, -742.33) * mm, "end": v(-461.01, -737.57) * mm});
            skSolve(sketch);
        }
        {
            var Q0;
            Q0=makeQuery(id+"F42.imprint","IMPRINT",FACE,{"disambiguationData":[TD([[makeQuery(id+"F42.imprint","IMPRINT",EDGE,{"derivedFrom":sQuery(id+"F42.wireOp",EDGE,"E168.bottom")}),1.0]])]});
            extrude(context, id + "F43", {"entities" : qUnion([Q0]), "operationType" : NewBodyOperationType.ADD, "depth" : 33.02 * mm});
        }
        {
            var Q0;
            Q0=makeQuery(id+"F43.boolean.opBoolean","MERGE",FACE,{"derivedFrom":[makeQuery(id+"F41.boolean.opBoolean","MERGE",FACE,{"derivedFrom":[makeQuery(id+"F31.opExtrude","SWEPT_FACE",FACE,{"disambiguationData":[OSD([sQuery(id+"F30.wireOp",EDGE,"E147.top")])]}),makeQuery(id+"F41.opExtrude","SWEPT_FACE",FACE,{"disambiguationData":[OSD([sQuery(id+"F40.wireOp",EDGE,"E161.bottom")])]})]}),makeQuery(id+"F43.opExtrude","SWEPT_FACE",FACE,{"disambiguationData":[OSD([sQuery(id+"F42.wireOp",EDGE,"E168.top")])]})]});
            var sketch = newSketch(context, id + "F44", { "sketchPlane" : qUnion([Q0])});
            skCircle(sketch, "E169", {"center": v(-479.55, -21.27) * mm, "radius": 3.97 * mm});
            skPoint(sketch, "E169.centerSnap0", {"position": v(-479.55, -37.78) * mm});
            skSolve(sketch);
        }
        {
            var Q0;
            Q0=makeQuery(id+"F44.imprint","IMPRINT",FACE,{"disambiguationData":[TD([[makeQuery(id+"F44.imprint","IMPRINT",EDGE,{"derivedFrom":sQuery(id+"F44.wireOp",EDGE,"E169")}),1.0]])]});
            extrude(context, id + "F45", {"entities" : qUnion([Q0]), "operationType" : NewBodyOperationType.REMOVE, "endBound" : BoundingType.UP_TO_NEXT, "oppositeDirection" : true, "depth" : 25.4 * mm});
        }
        {
            var Q0;
            Q0=makeQuery(id+"F33.boolean.opBoolean","MERGE",FACE,{"derivedFrom":[makeQuery(id+"F29.opExtrude","SWEPT_FACE",FACE,{"disambiguationData":[OSD([sQuery(id+"F28.wireOp",EDGE,"E143.top")])]}),makeQuery(id+"F33.opExtrude","SWEPT_FACE",FACE,{"disambiguationData":[OSD([sQuery(id+"F32.wireOp",EDGE,"E149.bottom")])]})]});
            var sketch = newSketch(context, id + "F46", { "sketchPlane" : qUnion([Q0])});
            skSolve(sketch);
        }
        {
            var Q0;
            {var subQ0=sQuery(id+"F28.wireOp",EDGE,"E143.top");Q0=makeQuery(id+"F46.imprint","IMPRINT",FACE,{"disambiguationData":[TD([[makeQuery(id+"F46.imprint","IMPRINT",EDGE,{"derivedFrom":makeQuery(id+"F29.opExtrude","CAP_EDGE",EDGE,{"disambiguationData":[OSD([subQ0])],"isStart":false})}),1.0]])]});}
            var sketch = newSketch(context, id + "F47", { "sketchPlane" : qUnion([Q0])});
            skCircle(sketch, "E170", {"center": v(-501.27, 73.03) * mm, "radius": 3.97 * mm});
            skSolve(sketch);
        }
        {
            var Q0;
            Q0 = qSketchRegion(id + "F47", true);
            extrude(context, id + "F48", {"entities" : qUnion([Q0]), "operationType" : NewBodyOperationType.REMOVE, "endBound" : BoundingType.THROUGH_ALL, "oppositeDirection" : true, "depth" : 25.4 * mm});
        }
        {
            var Q0;
            Q0=qCreatedBy(makeId("Top.planeOp"),FACE);
            var sketch = newSketch(context, id + "F49", { "sketchPlane" : qUnion([Q0])});
            skLineSegment(sketch, "E171.bottom", {"start": v(-298.81, -182.03) * mm, "end": v(-216.26, -182.03) * mm});
            skLineSegment(sketch, "E171.top", {"start": v(-298.81, -258.23) * mm, "end": v(-216.26, -258.23) * mm});
            skLineSegment(sketch, "E171.left", {"start": v(-298.81, -182.03) * mm, "end": v(-298.81, -258.23) * mm});
            skLineSegment(sketch, "E171.right", {"start": v(-216.26, -182.03) * mm, "end": v(-216.26, -258.23) * mm});
            skSolve(sketch);
        }
        {
            var Q0;
            Q0=makeQuery(id+"F49.imprint","IMPRINT",FACE,{"disambiguationData":[TD([[makeQuery(id+"F49.imprint","IMPRINT",EDGE,{"derivedFrom":sQuery(id+"F49.wireOp",EDGE,"E171.bottom")}),-1.0]])]});
            extrude(context, id + "F50", {"entities" : qUnion([Q0]), "depth" : 25.4 * mm});
        }
        {
            var Q0;
            Q0=makeQuery(id+"F50.opExtrude","SWEPT_FACE",FACE,{"disambiguationData":[OSD([sQuery(id+"F49.wireOp",EDGE,"E171.top")])]});
            var sketch = newSketch(context, id + "F51", { "sketchPlane" : qUnion([Q0])});
            skCircle(sketch, "E172", {"center": v(-222.61, 6.35) * mm, "radius": 3.97 * mm});
            skCircle(sketch, "E173", {"center": v(-222.61, 6.35) * mm, "radius": 6.35 * mm});
            skLineSegment(sketch, "E174", {"start": v(-228.96, 6.35) * mm, "end": v(-228.96, 12.7) * mm});
            skLineSegment(sketch, "E175", {"start": v(-228.96, 12.7) * mm, "end": v(-298.81, 12.7) * mm});
            skLineSegment(sketch, "E176", {"start": v(-298.81, 15.87) * mm, "end": v(-216.26, 15.88) * mm});
            skCircle(sketch, "E177", {"center": v(-228.96, 19.05) * mm, "radius": 1.9 * mm});
            skCircle(sketch, "E178.1.0.0", {"center": v(-244.96, 19.05) * mm, "radius": 1.9 * mm});
            skCircle(sketch, "E178.2.0.0", {"center": v(-260.96, 19.05) * mm, "radius": 1.9 * mm});
            skCircle(sketch, "E178.3.0.0", {"center": v(-276.96, 19.05) * mm, "radius": 1.9 * mm});
            skCircle(sketch, "E178.4.0.0", {"center": v(-292.96, 19.05) * mm, "radius": 1.9 * mm});
            skLineSegment(sketch, "E178.direction1", {"start": v(-228.96, 19.05) * mm, "end": v(-244.96, 19.05) * mm, "construction": true});
            skLineSegment(sketch, "E179.bottom", {"start": v(-299.31, 15.87) * mm, "end": v(-222.61, 15.87) * mm});
            skLineSegment(sketch, "E179.top", {"start": v(-299.31, 22.23) * mm, "end": v(-222.61, 22.23) * mm});
            skLineSegment(sketch, "E179.left", {"start": v(-299.31, 15.87) * mm, "end": v(-299.31, 22.23) * mm});
            skLineSegment(sketch, "E179.right", {"start": v(-222.61, 15.88) * mm, "end": v(-222.61, 22.23) * mm});
            skSolve(sketch);
        }
        {
            var Q0;
            Q0=makeQuery(id+"F51.imprint","IMPRINT",FACE,{"disambiguationData":[TD([[makeQuery(id+"F51.imprint","IMPRINT",EDGE,{"derivedFrom":sQuery(id+"F51.wireOp",EDGE,"E179.top")}),1.0]])]});
            var Q1;
            Q1=makeQuery(id+"F51.imprint","IMPRINT",FACE,{"disambiguationData":[TD([[makeQuery(id+"F51.imprint","IMPRINT",EDGE,{"derivedFrom":sQuery(id+"F51.wireOp",EDGE,"E178.3.0.0")}),1.0]])]});
            var Q2;
            Q2=makeQuery(id+"F51.imprint","IMPRINT",FACE,{"disambiguationData":[TD([[makeQuery(id+"F51.imprint","IMPRINT",EDGE,{"derivedFrom":sQuery(id+"F51.wireOp",EDGE,"E178.4.0.0")}),1.0]])]});
            var Q3;
            Q3=makeQuery(id+"F51.imprint","IMPRINT",FACE,{"disambiguationData":[TD([[makeQuery(id+"F51.imprint","IMPRINT",EDGE,{"derivedFrom":sQuery(id+"F51.wireOp",EDGE,"E178.2.0.0")}),1.0]])]});
            var Q4;
            Q4=makeQuery(id+"F51.imprint","IMPRINT",FACE,{"disambiguationData":[TD([[makeQuery(id+"F51.imprint","IMPRINT",EDGE,{"derivedFrom":sQuery(id+"F51.wireOp",EDGE,"E178.1.0.0")}),1.0]])]});
            var Q5;
            Q5=makeQuery(id+"F51.imprint","IMPRINT",FACE,{"disambiguationData":[TD([[makeQuery(id+"F51.imprint","IMPRINT",EDGE,{"derivedFrom":sQuery(id+"F51.wireOp",EDGE,"E177")}),1.0]])]});
            var Q6;
            Q6=makeQuery(id+"F51.imprint","IMPRINT",FACE,{"disambiguationData":[TD([[makeQuery(id+"F51.imprint","IMPRINT",EDGE,{"derivedFrom":sQuery(id+"F51.wireOp",EDGE,"E172")}),1.0]])]});
            var Q7;
            {var subQ5=sQuery(id+"F51.wireOp",EDGE,"E174");Q7=makeQuery(id+"F51.imprint","IMPRINT",FACE,{"disambiguationData":[TD([[makeQuery(id+"F51.imprint","IMPRINT",EDGE,{"derivedFrom":subQ5}),1.0]])]});}
            var Q8;
            {var subQ0=sQuery(id+"F51.wireOp",EDGE,"E173");var subQ1=sQuery(id+"F49.wireOp",EDGE,"E171.top");var subQ4=makeQuery(id+"F50.opExtrude","CAP_EDGE",EDGE,{"disambiguationData":[OSD([subQ1])],"isStart":true});var subQ5=makeQuery(id+"F51.imprint","INTERSECT",VERTEX,{"derivedFrom":[subQ4,subQ0]});Q8=makeQuery(id+"F51.imprint","IMPRINT",FACE,{"disambiguationData":[TD([[makeQuery(id+"F51.imprint","IMPRINT",EDGE,{"disambiguationData":[TD([[subQ5,-1.0]])],"derivedFrom":subQ0}),-1.0]])]});}
            extrude(context, id + "F52", {"entities" : qUnion([Q0, Q1, Q2, Q3, Q4, Q5, Q6, Q7, Q8]), "operationType" : NewBodyOperationType.REMOVE, "endBound" : BoundingType.UP_TO_NEXT, "oppositeDirection" : true, "depth" : 25.4 * mm});
        }
        {
            var Q0;
            Q0=makeQuery(id+"F43.boolean.opBoolean","MERGE",FACE,{"derivedFrom":[makeQuery(id+"F31.boolean.opBoolean","MERGE",FACE,{"derivedFrom":[makeQuery(id+"F29.opExtrude","SWEPT_FACE",FACE,{"disambiguationData":[OSD([sQuery(id+"F28.wireOp",EDGE,"E143.bottom")])]}),makeQuery(id+"F31.opExtrude","SWEPT_FACE",FACE,{"disambiguationData":[OSD([sQuery(id+"F30.wireOp",EDGE,"E147.bottom")])]})]}),makeQuery(id+"F43.opExtrude","SWEPT_FACE",FACE,{"disambiguationData":[OSD([sQuery(id+"F42.wireOp",EDGE,"E168.bottom")])]})]});
            var sketch = newSketch(context, id + "F53", { "sketchPlane" : qUnion([Q0])});
            skLineSegment(sketch, "E180.bottom", {"start": v(79, 152.4) * mm, "end": v(155.2, 152.4) * mm});
            skLineSegment(sketch, "E180.top", {"start": v(79, 101.6) * mm, "end": v(155.2, 101.6) * mm});
            skLineSegment(sketch, "E180.left", {"start": v(79, 152.4) * mm, "end": v(79, 101.6) * mm});
            skLineSegment(sketch, "E180.right", {"start": v(155.2, 152.4) * mm, "end": v(155.2, 101.6) * mm});
            skLineSegment(sketch, "E181.bottom", {"start": v(510.8, 152.4) * mm, "end": v(434.6, 152.4) * mm});
            skLineSegment(sketch, "E181.top", {"start": v(510.8, 101.6) * mm, "end": v(434.6, 101.6) * mm});
            skLineSegment(sketch, "E181.left", {"start": v(510.8, 152.4) * mm, "end": v(510.8, 101.6) * mm});
            skLineSegment(sketch, "E181.right", {"start": v(434.6, 152.4) * mm, "end": v(434.6, 101.6) * mm});
            skSolve(sketch);
        }
        {
            var Q0;
            Q0=makeQuery(id+"F53.imprint","IMPRINT",FACE,{"disambiguationData":[TD([[makeQuery(id+"F53.imprint","IMPRINT",EDGE,{"derivedFrom":sQuery(id+"F53.wireOp",EDGE,"E180.bottom")}),1.0]])]});
            var Q1;
            Q1=makeQuery(id+"F53.imprint","IMPRINT",FACE,{"disambiguationData":[TD([[makeQuery(id+"F53.imprint","IMPRINT",EDGE,{"derivedFrom":sQuery(id+"F53.wireOp",EDGE,"E181.bottom")}),1.0]])]});
            extrude(context, id + "F54", {"entities" : qUnion([Q0, Q1]), "operationType" : NewBodyOperationType.REMOVE, "endBound" : BoundingType.UP_TO_NEXT, "oppositeDirection" : true, "depth" : 25.4 * mm});
        }
        {
            var Q0;
            Q0=makeQuery(id+"F50.opExtrude","SWEPT_FACE",FACE,{"disambiguationData":[OSD([sQuery(id+"F49.wireOp",EDGE,"E171.left")])]});
            var sketch = newSketch(context, id + "F55", { "sketchPlane" : qUnion([Q0])});
            skLineSegment(sketch, "E182.bottom", {"start": v(185.2, 22.23) * mm, "end": v(255.05, 22.23) * mm});
            skLineSegment(sketch, "E182.top", {"start": v(185.2, 15.88) * mm, "end": v(255.05, 15.88) * mm});
            skLineSegment(sketch, "E182.left", {"start": v(185.2, 22.23) * mm, "end": v(185.2, 15.88) * mm});
            skLineSegment(sketch, "E182.right", {"start": v(255.05, 22.23) * mm, "end": v(255.05, 15.88) * mm});
            skSolve(sketch);
        }
        {
            var Q0;
            Q0=makeQuery(id+"F55.imprint","IMPRINT",FACE,{"disambiguationData":[TD([[makeQuery(id+"F55.imprint","IMPRINT",EDGE,{"derivedFrom":sQuery(id+"F55.wireOp",EDGE,"E182.bottom")}),-1.0]])]});
            var Q1;
            Q1=makeQuery(id+"F50.opExtrude","SWEPT_BODY",BODY,{"disambiguationData":[OSD([sQuery(id+"F49.wireOp",EDGE,"E171.bottom"),sQuery(id+"F49.wireOp",EDGE,"E171.top"),sQuery(id+"F49.wireOp",EDGE,"E171.left"),sQuery(id+"F49.wireOp",EDGE,"E171.right")])]});
            extrude(context, id + "F56", {"entities" : qUnion([Q0]), "operationType" : NewBodyOperationType.REMOVE, "endBound" : BoundingType.UP_TO_BODY, "oppositeDirection" : true, "endBoundEntityBody" : qUnion([Q1]), "depth" : 25.4 * mm});
        }
        {
            var Q0;
            Q0=makeQuery(id+"F33.boolean.opBoolean","MERGE",FACE,{"derivedFrom":[makeQuery(id+"F29.opExtrude","SWEPT_FACE",FACE,{"disambiguationData":[OSD([sQuery(id+"F28.wireOp",EDGE,"E143.top")])]}),makeQuery(id+"F33.opExtrude","SWEPT_FACE",FACE,{"disambiguationData":[OSD([sQuery(id+"F32.wireOp",EDGE,"E149.bottom")])]})]});
            var sketch = newSketch(context, id + "F57", { "sketchPlane" : qUnion([Q0])});
            skLineSegment(sketch, "E183.bottom", {"start": v(-491.75, 82.55) * mm, "end": v(-440.95, 82.55) * mm});
            skLineSegment(sketch, "E183.top", {"start": v(-491.75, 44.45) * mm, "end": v(-440.95, 44.45) * mm});
            skLineSegment(sketch, "E183.left", {"start": v(-491.75, 82.55) * mm, "end": v(-491.75, 44.45) * mm});
            skLineSegment(sketch, "E183.right", {"start": v(-440.95, 82.55) * mm, "end": v(-440.95, 44.45) * mm});
            skLineSegment(sketch, "E184.bottom", {"start": v(-98.05, 82.55) * mm, "end": v(-148.85, 82.55) * mm});
            skLineSegment(sketch, "E184.top", {"start": v(-98.05, 44.45) * mm, "end": v(-148.85, 44.45) * mm});
            skLineSegment(sketch, "E184.left", {"start": v(-98.05, 82.55) * mm, "end": v(-98.05, 44.45) * mm});
            skLineSegment(sketch, "E184.right", {"start": v(-148.85, 82.55) * mm, "end": v(-148.85, 44.45) * mm});
            skSolve(sketch);
        }
        {
            var Q0;
            Q0=makeQuery(id+"F57.imprint","IMPRINT",FACE,{"disambiguationData":[TD([[makeQuery(id+"F57.imprint","IMPRINT",EDGE,{"derivedFrom":sQuery(id+"F57.wireOp",EDGE,"E183.bottom")}),-1.0]])]});
            var Q1;
            Q1=makeQuery(id+"F57.imprint","IMPRINT",FACE,{"disambiguationData":[TD([[makeQuery(id+"F57.imprint","IMPRINT",EDGE,{"derivedFrom":sQuery(id+"F57.wireOp",EDGE,"E184.bottom")}),-1.0]])]});
            var Q2;
            Q2=makeQuery(id+"F41.boolean.opBoolean","MERGE",FACE,{"derivedFrom":[makeQuery(id+"F33.opExtrude","SWEPT_FACE",FACE,{"disambiguationData":[OSD([sQuery(id+"F32.wireOp",EDGE,"E149.top")])]}),makeQuery(id+"F41.opExtrude","SWEPT_FACE",FACE,{"disambiguationData":[OSD([sQuery(id+"F40.wireOp",EDGE,"E162.top")])]})]});
            extrude(context, id + "F58", {"entities" : qUnion([Q0, Q1]), "operationType" : NewBodyOperationType.REMOVE, "endBound" : BoundingType.UP_TO_SURFACE, "oppositeDirection" : true, "endBoundEntityFace" : qUnion([Q2]), "depth" : 25.4 * mm});
        }
        {
            var Q0;
            Q0=makeQuery(id+"F33.boolean.opBoolean","MERGE",FACE,{"derivedFrom":[makeQuery(id+"F31.boolean.opBoolean","MERGE",FACE,{"derivedFrom":[makeQuery(id+"F29.opExtrude","SWEPT_FACE",FACE,{"disambiguationData":[OSD([sQuery(id+"F28.wireOp",EDGE,"E143.right")])]}),makeQuery(id+"F31.opExtrude","SWEPT_FACE",FACE,{"disambiguationData":[OSD([sQuery(id+"F30.wireOp",EDGE,"E147.right")])]})]}),makeQuery(id+"F33.opExtrude","SWEPT_FACE",FACE,{"disambiguationData":[OSD([sQuery(id+"F32.wireOp",EDGE,"E149.right")])]})]});
            var sketch = newSketch(context, id + "F59", { "sketchPlane" : qUnion([Q0])});
            skLineSegment(sketch, "E185.bottom", {"start": v(648.98, -4.76) * mm, "end": v(742.33, -4.76) * mm});
            skLineSegment(sketch, "E185.top", {"start": v(648.98, 0) * mm, "end": v(742.33, 0) * mm});
            skLineSegment(sketch, "E185.left", {"start": v(648.98, -4.76) * mm, "end": v(648.98, 0) * mm});
            skLineSegment(sketch, "E185.right", {"start": v(742.33, -4.76) * mm, "end": v(742.33, 0) * mm});
            skSolve(sketch);
        }
        {
            var Q0;
            Q0=makeQuery(id+"F59.imprint","IMPRINT",FACE,{"disambiguationData":[TD([[makeQuery(id+"F59.imprint","IMPRINT",EDGE,{"derivedFrom":sQuery(id+"F59.wireOp",EDGE,"E185.bottom")}),-1.0]])]});
            extrude(context, id + "F60", {"entities" : qUnion([Q0]), "operationType" : NewBodyOperationType.ADD, "depth" : 4.76 * mm});
        }
        {
            var Q0;
            Q0=makeQuery(id+"F60.boolean.opBoolean","MERGE",FACE,{"derivedFrom":[makeQuery(id+"F29.opExtrude","CAP_FACE",FACE,{"disambiguationData":[OSD([sQuery(id+"F28.wireOp",EDGE,"E143.bottom"),sQuery(id+"F28.wireOp",EDGE,"E143.top"),sQuery(id+"F28.wireOp",EDGE,"E143.left"),sQuery(id+"F28.wireOp",EDGE,"E143.right"),sQuery(id+"F28.wireOp",EDGE,"E144"),sQuery(id+"F28.wireOp",EDGE,"E145"),sQuery(id+"F28.wireOp",EDGE,"E146")])],"isStart":true}),makeQuery(id+"F60.opExtrude","SWEPT_FACE",FACE,{"disambiguationData":[OSD([sQuery(id+"F59.wireOp",EDGE,"E185.top")])]})]});
            var sketch = newSketch(context, id + "F61", { "sketchPlane" : qUnion([Q0])});
            skLineSegment(sketch, "E186.bottom", {"start": v(-74.23, 742.33) * mm, "end": v(-78.74, 742.33) * mm});
            skLineSegment(sketch, "E186.top", {"start": v(-74.23, 648.98) * mm, "end": v(-78.74, 648.98) * mm});
            skLineSegment(sketch, "E186.left", {"start": v(-74.23, 742.33) * mm, "end": v(-74.23, 648.98) * mm});
            skLineSegment(sketch, "E186.right", {"start": v(-78.74, 742.33) * mm, "end": v(-78.74, 648.98) * mm});
            skSolve(sketch);
        }
        {
            var Q0;
            Q0=makeQuery(id+"F61.imprint","IMPRINT",FACE,{"disambiguationData":[TD([[makeQuery(id+"F61.imprint","IMPRINT",EDGE,{"derivedFrom":sQuery(id+"F61.wireOp",EDGE,"E186.bottom")}),1.0]])]});
            extrude(context, id + "F62", {"entities" : qUnion([Q0]), "operationType" : NewBodyOperationType.ADD, "depth" : 76.2 * mm});
        }
        {
            var Q0;
            Q0=makeQuery(id+"F23.opExtrude","CAP_FACE",FACE,{"disambiguationData":[OSD([sQuery(id+"F22.wireOp",EDGE,"E112.bottom"),sQuery(id+"F22.wireOp",EDGE,"E112.top"),sQuery(id+"F22.wireOp",EDGE,"E112.left"),sQuery(id+"F22.wireOp",EDGE,"E112.right"),sQuery(id+"F22.wireOp",EDGE,"E113.bottom"),sQuery(id+"F22.wireOp",EDGE,"E113.top"),sQuery(id+"F22.wireOp",EDGE,"E113.right"),sQuery(id+"F22.wireOp",EDGE,"E114.0.1.0"),sQuery(id+"F22.wireOp",EDGE,"E114.0.1.1"),sQuery(id+"F22.wireOp",EDGE,"E114.0.1.2"),sQuery(id+"F22.wireOp",EDGE,"E114.0.2.0"),sQuery(id+"F22.wireOp",EDGE,"E114.0.2.1"),sQuery(id+"F22.wireOp",EDGE,"E114.0.2.2"),sQuery(id+"F22.wireOp",EDGE,"E116.MirrorCS"),sQuery(id+"F22.wireOp",EDGE,"E117.MirrorCS"),sQuery(id+"F22.wireOp",EDGE,"E119.MirrorCS"),sQuery(id+"F22.wireOp",EDGE,"E120.MirrorCS"),sQuery(id+"F22.wireOp",EDGE,"E121.MirrorCS"),sQuery(id+"F22.wireOp",EDGE,"E122.MirrorCS"),sQuery(id+"F22.wireOp",EDGE,"E123.MirrorCS"),sQuery(id+"F22.wireOp",EDGE,"E124.MirrorCS"),sQuery(id+"F22.wireOp",EDGE,"E125.MirrorCS"),sQuery(id+"F22.wireOp",EDGE,"E126.top"),sQuery(id+"F22.wireOp",EDGE,"E126.left"),sQuery(id+"F22.wireOp",EDGE,"E126.right"),sQuery(id+"F22.wireOp",EDGE,"E127.1.0.0"),sQuery(id+"F22.wireOp",EDGE,"E127.1.0.1"),sQuery(id+"F22.wireOp",EDGE,"E127.1.0.2"),sQuery(id+"F22.wireOp",EDGE,"E127.2.0.0"),sQuery(id+"F22.wireOp",EDGE,"E127.2.0.1"),sQuery(id+"F22.wireOp",EDGE,"E127.2.0.2"),sQuery(id+"F22.wireOp",EDGE,"E127.3.0.0"),sQuery(id+"F22.wireOp",EDGE,"E127.3.0.1"),sQuery(id+"F22.wireOp",EDGE,"E127.3.0.2")])],"isStart":true});
            var sketch = newSketch(context, id + "F63", { "sketchPlane" : qUnion([Q0])});
            skLineSegment(sketch, "E187.bottom", {"start": v(-394.64, 96.41) * mm, "end": v(-374.32, 96.41) * mm});
            skLineSegment(sketch, "E187.top", {"start": v(-394.64, 54.76) * mm, "end": v(-374.32, 54.76) * mm});
            skLineSegment(sketch, "E187.left", {"start": v(-394.64, 96.41) * mm, "end": v(-394.64, 54.76) * mm});
            skLineSegment(sketch, "E187.right", {"start": v(-374.32, 96.41) * mm, "end": v(-374.32, 54.76) * mm});
            skCircle(sketch, "E188", {"center": v(-371, 98.58) * mm, "radius": 1.9 * mm});
            skCircle(sketch, "E189", {"center": v(-371, 79.53) * mm, "radius": 1.9 * mm});
            skCircle(sketch, "E190", {"center": v(-371, 52.59) * mm, "radius": 1.9 * mm});
            skLineSegment(sketch, "E191", {"start": v(-371, 98.58) * mm, "end": v(-371, 52.59) * mm, "construction": true});
            skLineSegment(sketch, "E192", {"start": v(-384.48, 96.41) * mm, "end": v(-384.48, 54.76) * mm, "construction": true});
            skLineSegment(sketch, "E193", {"start": v(-384.48, 75.59) * mm, "end": v(-371, 75.59) * mm, "construction": true});
            skCircle(sketch, "E194.MirrorC", {"center": v(-397.96, 98.58) * mm, "radius": 1.9 * mm});
            skCircle(sketch, "E195.MirrorC", {"center": v(-397.96, 79.53) * mm, "radius": 1.9 * mm});
            skCircle(sketch, "E196.MirrorC", {"center": v(-397.96, 52.59) * mm, "radius": 1.9 * mm});
            skLineSegment(sketch, "E197", {"start": v(-350.2, 105.94) * mm, "end": v(-350.2, 18.94) * mm});
            skLineSegment(sketch, "E198.MirrorCS", {"start": v(-315.9, 75.59) * mm, "end": v(-329.38, 75.59) * mm, "construction": true});
            skCircle(sketch, "E199.MirrorC", {"center": v(-302.43, 79.53) * mm, "radius": 1.9 * mm});
            skCircle(sketch, "E200.MirrorC", {"center": v(-302.43, 98.58) * mm, "radius": 1.9 * mm});
            skCircle(sketch, "E201.MirrorC", {"center": v(-302.43, 52.59) * mm, "radius": 1.9 * mm});
            skLineSegment(sketch, "E202.MirrorCS", {"start": v(-315.9, 96.41) * mm, "end": v(-315.9, 54.76) * mm, "construction": true});
            skLineSegment(sketch, "E203.MirrorCS", {"start": v(-329.38, 98.58) * mm, "end": v(-329.38, 52.59) * mm, "construction": true});
            skLineSegment(sketch, "E204.MirrorCS", {"start": v(-305.74, 96.41) * mm, "end": v(-326.06, 96.41) * mm});
            skLineSegment(sketch, "E205.MirrorCS", {"start": v(-305.74, 96.41) * mm, "end": v(-305.74, 54.76) * mm});
            skLineSegment(sketch, "E206.MirrorCS", {"start": v(-305.74, 54.76) * mm, "end": v(-326.06, 54.76) * mm});
            skCircle(sketch, "E207.MirrorC", {"center": v(-329.38, 98.58) * mm, "radius": 1.9 * mm});
            skLineSegment(sketch, "E208.MirrorCS", {"start": v(-326.06, 96.41) * mm, "end": v(-326.06, 54.76) * mm});
            skCircle(sketch, "E209.MirrorC", {"center": v(-329.38, 52.59) * mm, "radius": 1.9 * mm});
            skCircle(sketch, "E210.MirrorC", {"center": v(-329.38, 79.53) * mm, "radius": 1.9 * mm});
            skSolve(sketch);
        }
        {
            var Q0;
            Q0 = qSketchRegion(id + "F63", true);
            extrude(context, id + "F64", {"entities" : qUnion([Q0]), "operationType" : NewBodyOperationType.REMOVE, "endBound" : BoundingType.UP_TO_NEXT, "oppositeDirection" : true, "depth" : 25.4 * mm});
        }
        {
            var Q0;
            Q0=makeQuery(id+"F62.boolean.opBoolean","MERGE",FACE,{"derivedFrom":[makeQuery(id+"F60.boolean.opBoolean","MERGE",FACE,{"derivedFrom":[makeQuery(id+"F33.boolean.opBoolean","MERGE",FACE,{"derivedFrom":[makeQuery(id+"F29.opExtrude","SWEPT_FACE",FACE,{"disambiguationData":[OSD([sQuery(id+"F28.wireOp",EDGE,"E143.top")])]}),makeQuery(id+"F33.opExtrude","SWEPT_FACE",FACE,{"disambiguationData":[OSD([sQuery(id+"F32.wireOp",EDGE,"E149.bottom")])]})]}),makeQuery(id+"F60.opExtrude","SWEPT_FACE",FACE,{"disambiguationData":[OSD([sQuery(id+"F59.wireOp",EDGE,"E185.left")])]})]}),makeQuery(id+"F62.opExtrude","SWEPT_FACE",FACE,{"disambiguationData":[OSD([sQuery(id+"F61.wireOp",EDGE,"E186.top")])]})]});
            var sketch = newSketch(context, id + "F65", { "sketchPlane" : qUnion([Q0])});
            skLineSegment(sketch, "E211", {"start": v(-510.8, 48.29) * mm, "end": v(-89.4, 48.29) * mm, "construction": true});
            skLineSegment(sketch, "E212", {"start": v(-89.4, 48.29) * mm, "end": v(-89.4, 3.96) * mm, "construction": true});
            skCircle(sketch, "E213", {"center": v(-89.4, 3.96) * mm, "radius": 1.9 * mm});
            skCircle(sketch, "E214.1.0.0", {"center": v(-121.4, 3.96) * mm, "radius": 1.9 * mm});
            skCircle(sketch, "E214.2.0.0", {"center": v(-153.4, 3.96) * mm, "radius": 1.9 * mm});
            skCircle(sketch, "E214.3.0.0", {"center": v(-185.4, 3.96) * mm, "radius": 1.9 * mm});
            skCircle(sketch, "E214.4.0.0", {"center": v(-217.4, 3.96) * mm, "radius": 1.9 * mm});
            skCircle(sketch, "E214.5.0.0", {"center": v(-249.4, 3.96) * mm, "radius": 1.9 * mm});
            skCircle(sketch, "E214.6.0.0", {"center": v(-281.4, 3.96) * mm, "radius": 1.9 * mm});
            skCircle(sketch, "E214.7.0.0", {"center": v(-313.4, 3.96) * mm, "radius": 1.9 * mm});
            skCircle(sketch, "E214.8.0.0", {"center": v(-345.4, 3.96) * mm, "radius": 1.9 * mm});
            skCircle(sketch, "E214.9.0.0", {"center": v(-377.4, 3.96) * mm, "radius": 1.9 * mm});
            skLineSegment(sketch, "E214.direction1", {"start": v(-89.4, 3.96) * mm, "end": v(-121.4, 3.96) * mm, "construction": true});
            skSolve(sketch);
        }
        {
            var Q0;
            Q0 = qSketchRegion(id + "F65", true);
            var Q1;
            Q1=makeQuery(id+"F41.boolean.opBoolean","MERGE",FACE,{"derivedFrom":[makeQuery(id+"F33.opExtrude","SWEPT_FACE",FACE,{"disambiguationData":[OSD([sQuery(id+"F32.wireOp",EDGE,"E149.top")])]}),makeQuery(id+"F41.opExtrude","SWEPT_FACE",FACE,{"disambiguationData":[OSD([sQuery(id+"F40.wireOp",EDGE,"E162.top")])]})]});
            extrude(context, id + "F66", {"entities" : qUnion([Q0]), "operationType" : NewBodyOperationType.REMOVE, "endBound" : BoundingType.UP_TO_SURFACE, "oppositeDirection" : true, "endBoundEntityFace" : qUnion([Q1]), "depth" : 25.4 * mm});
        }
        {
            var Q0;
            Q0=makeQuery(id+"F23.opExtrude","CAP_FACE",FACE,{"disambiguationData":[OSD([sQuery(id+"F22.wireOp",EDGE,"E112.bottom"),sQuery(id+"F22.wireOp",EDGE,"E112.top"),sQuery(id+"F22.wireOp",EDGE,"E112.left"),sQuery(id+"F22.wireOp",EDGE,"E112.right"),sQuery(id+"F22.wireOp",EDGE,"E113.bottom"),sQuery(id+"F22.wireOp",EDGE,"E113.top"),sQuery(id+"F22.wireOp",EDGE,"E113.right"),sQuery(id+"F22.wireOp",EDGE,"E114.0.1.0"),sQuery(id+"F22.wireOp",EDGE,"E114.0.1.1"),sQuery(id+"F22.wireOp",EDGE,"E114.0.1.2"),sQuery(id+"F22.wireOp",EDGE,"E114.0.2.0"),sQuery(id+"F22.wireOp",EDGE,"E114.0.2.1"),sQuery(id+"F22.wireOp",EDGE,"E114.0.2.2"),sQuery(id+"F22.wireOp",EDGE,"E116.MirrorCS"),sQuery(id+"F22.wireOp",EDGE,"E117.MirrorCS"),sQuery(id+"F22.wireOp",EDGE,"E119.MirrorCS"),sQuery(id+"F22.wireOp",EDGE,"E120.MirrorCS"),sQuery(id+"F22.wireOp",EDGE,"E121.MirrorCS"),sQuery(id+"F22.wireOp",EDGE,"E122.MirrorCS"),sQuery(id+"F22.wireOp",EDGE,"E123.MirrorCS"),sQuery(id+"F22.wireOp",EDGE,"E124.MirrorCS"),sQuery(id+"F22.wireOp",EDGE,"E125.MirrorCS"),sQuery(id+"F22.wireOp",EDGE,"E126.top"),sQuery(id+"F22.wireOp",EDGE,"E126.left"),sQuery(id+"F22.wireOp",EDGE,"E126.right"),sQuery(id+"F22.wireOp",EDGE,"E127.1.0.0"),sQuery(id+"F22.wireOp",EDGE,"E127.1.0.1"),sQuery(id+"F22.wireOp",EDGE,"E127.1.0.2"),sQuery(id+"F22.wireOp",EDGE,"E127.2.0.0"),sQuery(id+"F22.wireOp",EDGE,"E127.2.0.1"),sQuery(id+"F22.wireOp",EDGE,"E127.2.0.2"),sQuery(id+"F22.wireOp",EDGE,"E127.3.0.0"),sQuery(id+"F22.wireOp",EDGE,"E127.3.0.1"),sQuery(id+"F22.wireOp",EDGE,"E127.3.0.2")])],"isStart":true});
            var sketch = newSketch(context, id + "F67", { "sketchPlane" : qUnion([Q0])});
            skLineSegment(sketch, "E215", {"start": v(-371, 98.58) * mm, "end": v(-371, 79.53) * mm, "construction": true});
            skCircle(sketch, "E216", {"center": v(-384.48, 89.06) * mm, "radius": 37.6 * mm});
            skPoint(sketch, "E216.centerSnap0", {"position": v(-371, 89.06) * mm});
            skPoint(sketch, "E216.centerSnap1", {"position": v(-384.48, 96.41) * mm});
            skSolve(sketch);
        }
        {
            var Q0;
            {var subQ0=sQuery(id+"F22.wireOp",EDGE,"E113.bottom");Q0=makeQuery(id+"F67.imprint","IMPRINT",FACE,{"disambiguationData":[TD([[makeQuery(id+"F67.imprint","IMPRINT",EDGE,{"derivedFrom":makeQuery(id+"F23.opExtrude","CAP_EDGE",EDGE,{"disambiguationData":[OSD([subQ0])],"isStart":true})}),1.0]])]});}
            var Q1;
            {var subQ1=sQuery(id+"F22.wireOp",EDGE,"E113.bottom");Q1=makeQuery(id+"F67.imprint","IMPRINT",FACE,{"disambiguationData":[TD([[makeQuery(id+"F67.imprint","IMPRINT",EDGE,{"derivedFrom":makeQuery(id+"F23.opExtrude","CAP_EDGE",EDGE,{"disambiguationData":[OSD([subQ1])],"isStart":true})}),-1.0]])]});}
            var Q2;
            Q2=makeQuery(id+"F67.imprint","IMPRINT",FACE,{"disambiguationData":[TD([[makeQuery(id+"F67.imprint","IMPRINT",EDGE,{"derivedFrom":makeQuery(id+"F64.boolean.opBoolean","COPY",EDGE,{"derivedFrom":makeQuery(id+"F64.opExtrude","CAP_EDGE",EDGE,{"disambiguationData":[OSD([sQuery(id+"F63.wireOp",EDGE,"E187.bottom")])],"isStart":true})})}),-1.0]])]});
            var Q3;
            Q3=makeQuery(id+"F67.imprint","IMPRINT",FACE,{"disambiguationData":[TD([[makeQuery(id+"F67.imprint","IMPRINT",EDGE,{"derivedFrom":makeQuery(id+"F64.boolean.opBoolean","COPY",EDGE,{"derivedFrom":makeQuery(id+"F64.opExtrude","CAP_EDGE",EDGE,{"disambiguationData":[OSD([sQuery(id+"F63.wireOp",EDGE,"E189")])],"isStart":true})})}),1.0]])]});
            var Q4;
            Q4=makeQuery(id+"F67.imprint","IMPRINT",FACE,{"disambiguationData":[TD([[makeQuery(id+"F67.imprint","IMPRINT",EDGE,{"derivedFrom":makeQuery(id+"F64.boolean.opBoolean","COPY",EDGE,{"derivedFrom":makeQuery(id+"F64.opExtrude","CAP_EDGE",EDGE,{"disambiguationData":[OSD([sQuery(id+"F63.wireOp",EDGE,"E188")])],"isStart":true})})}),1.0]])]});
            var Q5;
            Q5=makeQuery(id+"F67.imprint","IMPRINT",FACE,{"disambiguationData":[TD([[makeQuery(id+"F67.imprint","IMPRINT",EDGE,{"derivedFrom":makeQuery(id+"F64.boolean.opBoolean","COPY",EDGE,{"derivedFrom":makeQuery(id+"F64.opExtrude","CAP_EDGE",EDGE,{"disambiguationData":[OSD([sQuery(id+"F63.wireOp",EDGE,"E195.MirrorC")])],"isStart":true})})}),-1.0]])]});
            var Q6;
            Q6=makeQuery(id+"F67.imprint","IMPRINT",FACE,{"disambiguationData":[TD([[makeQuery(id+"F67.imprint","IMPRINT",EDGE,{"derivedFrom":makeQuery(id+"F64.boolean.opBoolean","COPY",EDGE,{"derivedFrom":makeQuery(id+"F64.opExtrude","CAP_EDGE",EDGE,{"disambiguationData":[OSD([sQuery(id+"F63.wireOp",EDGE,"E194.MirrorC")])],"isStart":true})})}),-1.0]])]});
            extrude(context, id + "F68", {"entities" : qUnion([Q0, Q1, Q2, Q3, Q4, Q5, Q6]), "depth" : 25.4 * mm});
        }
        {
            var Q0;
            Q0=qCreatedBy(makeId("Top.planeOp"),FACE);
            var sketch = newSketch(context, id + "F69", { "sketchPlane" : qUnion([Q0])});
            skLineSegment(sketch, "E217.bottom", {"start": v(0, 109.6) * mm, "end": v(309.05, 109.6) * mm});
            skLineSegment(sketch, "E217.top", {"start": v(0, 135) * mm, "end": v(309.05, 135) * mm});
            skLineSegment(sketch, "E217.left", {"start": v(0, 109.6) * mm, "end": v(0, 135) * mm});
            skLineSegment(sketch, "E217.right", {"start": v(309.05, 109.6) * mm, "end": v(309.05, 135) * mm});
            skSolve(sketch);
        }
        {
            var Q0;
            Q0=makeQuery(id+"F69.imprint","IMPRINT",FACE,{"disambiguationData":[TD([[makeQuery(id+"F69.imprint","IMPRINT",EDGE,{"derivedFrom":sQuery(id+"F69.wireOp",EDGE,"E217.bottom")}),1.0]])]});
            extrude(context, id + "F70", {"entities" : qUnion([Q0]), "depth" : 4.76 * mm});
        }
        {
            var Q0;
            Q0=makeQuery(id+"F11.opExtrude","SWEPT_EDGE",EDGE,{"disambiguationData":[OSD([sQuery(id+"F10.wireOp",EDGE,"E40.left"),sQuery(id+"F10.wireOp",EDGE,"E41"),sQuery(id+"F10.wireOp",EDGE,"E48")])]});
            fillet(context, id + "F71", {"entities" : qUnion([Q0]), "radius" : 101.6 * mm, "tangentPropagation" : true, "allowEdgeOverflow" : false});
        }
        {
            var Q0;
            Q0=makeQuery(id+"F11.opExtrude","SWEPT_EDGE",EDGE,{"disambiguationData":[OSD([sQuery(id+"F10.wireOp",EDGE,"E43"),sQuery(id+"F10.wireOp",EDGE,"E53")])]});
            fillet(context, id + "F72", {"entities" : qUnion([Q0]), "radius" : 50.8 * mm, "tangentPropagation" : true, "allowEdgeOverflow" : false});
        }
        {
            var Q0;
            Q0=makeQuery(id+"F11.opExtrude","SWEPT_EDGE",EDGE,{"disambiguationData":[OSD([sQuery(id+"F10.wireOp",EDGE,"E40.top"),sQuery(id+"F10.wireOp",EDGE,"E40.right"),sQuery(id+"F10.wireOp",EDGE,"E50")])]});
            fillet(context, id + "F73", {"entities" : qUnion([Q0]), "radius" : 25.4 * mm, "tangentPropagation" : true, "allowEdgeOverflow" : false});
        }
        {
            var Q0;
            Q0=makeQuery(id+"F11.opExtrude","SWEPT_EDGE",EDGE,{"disambiguationData":[OSD([sQuery(id+"F10.wireOp",EDGE,"E40.right"),sQuery(id+"F10.wireOp",EDGE,"E48")])]});
            fillet(context, id + "F74", {"entities" : qUnion([Q0]), "radius" : 50.8 * mm, "tangentPropagation" : true, "allowEdgeOverflow" : false});
        }
        {
            var Q0;
            Q0=makeQuery(id+"F11.opExtrude","SWEPT_EDGE",EDGE,{"disambiguationData":[OSD([sQuery(id+"F10.wireOp",EDGE,"E48"),sQuery(id+"F10.wireOp",EDGE,"E52")])]});
            fillet(context, id + "F75", {"entities" : qUnion([Q0]), "radius" : 12.7 * mm, "tangentPropagation" : true, "allowEdgeOverflow" : false});
        }
        {
            var Q0;
            Q0=makeQuery(id+"F35.opExtrude","CAP_FACE",FACE,{"disambiguationData":[OSD([sQuery(id+"F34.wireOp",EDGE,"E150.bottom"),sQuery(id+"F34.wireOp",EDGE,"E150.top"),sQuery(id+"F34.wireOp",EDGE,"E150.left"),sQuery(id+"F34.wireOp",EDGE,"E150.right")])],"isStart":false});
            var sketch = newSketch(context, id + "F76", { "sketchPlane" : qUnion([Q0])});
            skLineSegment(sketch, "E218.bottom", {"start": v(406.4, 76.2) * mm, "end": v(177.8, 76.2) * mm});
            skLineSegment(sketch, "E218.top", {"start": v(406.4, 73.03) * mm, "end": v(177.8, 73.02) * mm});
            skLineSegment(sketch, "E218.left", {"start": v(406.4, 76.2) * mm, "end": v(406.4, 73.03) * mm});
            skLineSegment(sketch, "E218.right", {"start": v(177.8, 76.2) * mm, "end": v(177.8, 73.02) * mm});
            skLineSegment(sketch, "E219.bottom", {"start": v(406.4, 0) * mm, "end": v(177.8, 0) * mm});
            skLineSegment(sketch, "E219.top", {"start": v(406.4, 3.17) * mm, "end": v(177.8, 3.17) * mm});
            skLineSegment(sketch, "E219.left", {"start": v(406.4, 0) * mm, "end": v(406.4, 3.17) * mm});
            skLineSegment(sketch, "E219.right", {"start": v(177.8, 0) * mm, "end": v(177.8, 3.17) * mm});
            skSolve(sketch);
        }
        {
            var Q0;
            Q0=makeQuery(id+"F76.imprint","IMPRINT",FACE,{"disambiguationData":[TD([[makeQuery(id+"F76.imprint","IMPRINT",EDGE,{"derivedFrom":sQuery(id+"F76.wireOp",EDGE,"E219.bottom")}),1.0]])]});
            var Q1;
            Q1=makeQuery(id+"F76.imprint","IMPRINT",FACE,{"disambiguationData":[TD([[makeQuery(id+"F76.imprint","IMPRINT",EDGE,{"derivedFrom":sQuery(id+"F76.wireOp",EDGE,"E218.bottom")}),-1.0]])]});
            extrude(context, id + "F77", {"entities" : qUnion([Q0, Q1]), "operationType" : NewBodyOperationType.ADD, "depth" : 28.57 * mm});
        }
    });
